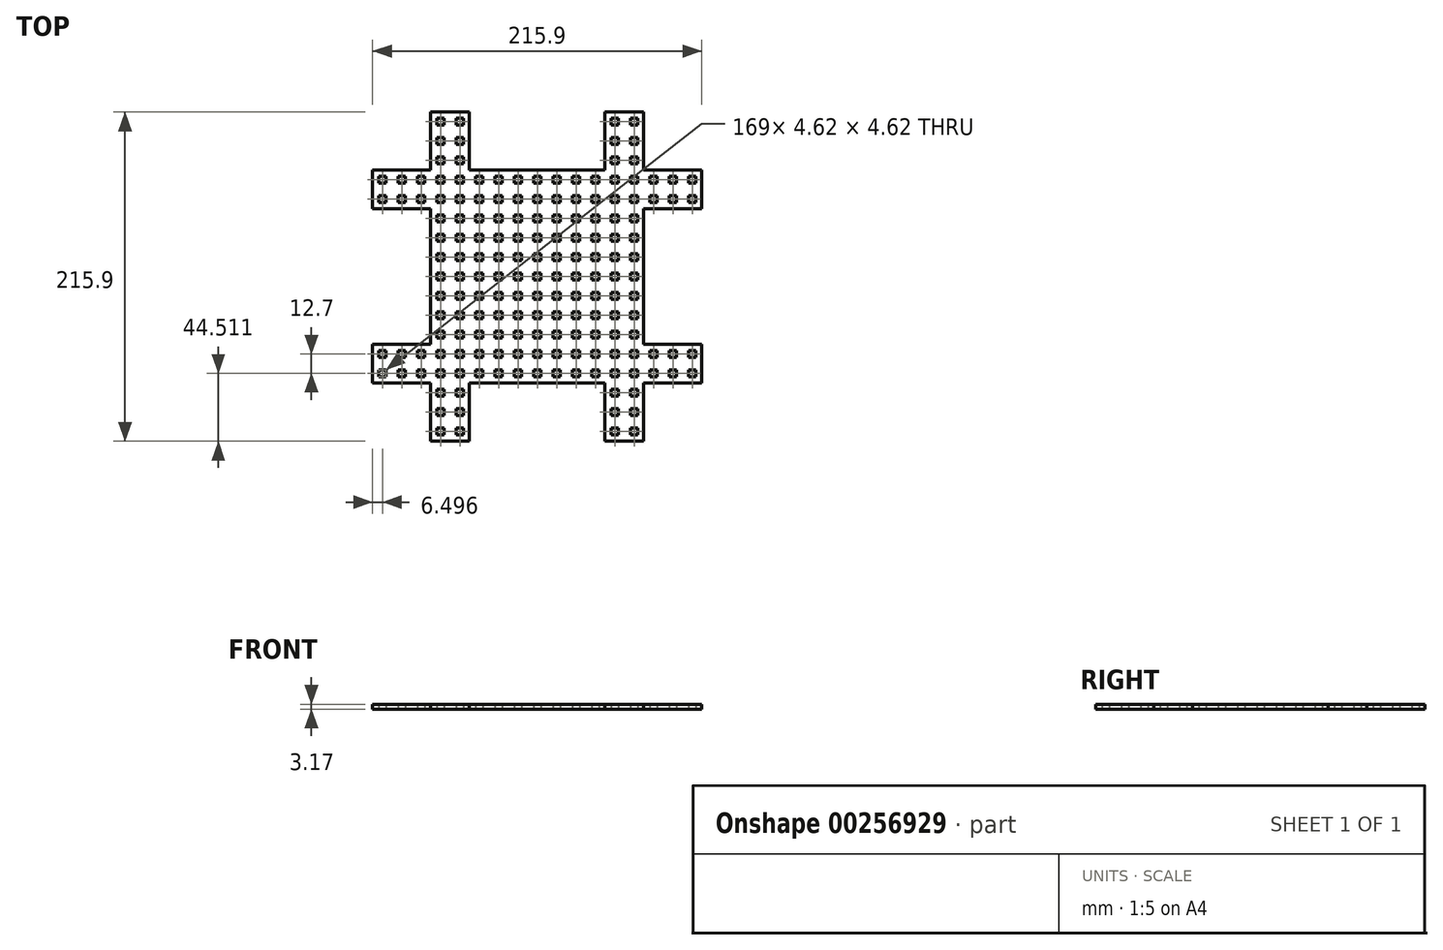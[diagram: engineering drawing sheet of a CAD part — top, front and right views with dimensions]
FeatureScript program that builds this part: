
annotation { "Feature Type Name" : "Feature", "Feature Type Description" : "" }
export const myFeature = defineFeature(function(context is Context, id is Id, definition is map)
    precondition{}
    {
        {
            var Q0;
            Q0=qCreatedBy(makeId("Top.planeOp"),FACE);
            var sketch = newSketch(context, id + "F0", { "sketchPlane" : qUnion([Q0])});
            skLineSegment(sketch, "E0.top", {"start": v(107.95, 44.45) * mm, "end": v(69.85, 44.45) * mm});
            skLineSegment(sketch, "E1.left", {"start": v(44.45, 107.95) * mm, "end": v(44.45, 69.85) * mm});
            skLineSegment(sketch, "E1.right", {"start": v(-44.45, 107.95) * mm, "end": v(-44.45, 69.85) * mm});
            skLineSegment(sketch, "E2.trimOffspring", {"start": v(-69.85, 44.45) * mm, "end": v(-107.95, 44.45) * mm});
            skLineSegment(sketch, "E3.trimOffspring", {"start": v(-69.85, -44.45) * mm, "end": v(-107.95, -44.45) * mm});
            skLineSegment(sketch, "E4.trimOffspring", {"start": v(-44.45, -69.85) * mm, "end": v(-44.45, -107.95) * mm});
            skLineSegment(sketch, "E5", {"start": v(-107.95, 44.45) * mm, "end": v(-69.85, 44.45) * mm});
            skLineSegment(sketch, "E6", {"start": v(-69.85, 69.85) * mm, "end": v(-69.85, 107.95) * mm});
            skLineSegment(sketch, "E7.bottom", {"start": v(-69.85, 107.95) * mm, "end": v(-44.45, 107.95) * mm});
            skLineSegment(sketch, "E7.top", {"start": v(-69.85, -107.95) * mm, "end": v(-44.45, -107.95) * mm});
            skLineSegment(sketch, "E7.left", {"start": v(-69.85, 107.95) * mm, "end": v(-69.85, 69.85) * mm});
            skLineSegment(sketch, "E7.right", {"start": v(69.85, 107.95) * mm, "end": v(69.85, 69.85) * mm});
            skLineSegment(sketch, "E8.bottom", {"start": v(107.95, -69.85) * mm, "end": v(69.85, -69.85) * mm});
            skLineSegment(sketch, "E8.left", {"start": v(107.95, -69.85) * mm, "end": v(107.95, -44.45) * mm});
            skLineSegment(sketch, "E9.trimOffspring", {"start": v(44.45, 107.95) * mm, "end": v(69.85, 107.95) * mm});
            skLineSegment(sketch, "E10.trimOffspring", {"start": v(44.45, 69.85) * mm, "end": v(-44.45, 69.85) * mm});
            skLineSegment(sketch, "E11.trimOffspring", {"start": v(69.85, 44.45) * mm, "end": v(69.85, -44.45) * mm});
            skLineSegment(sketch, "E12", {"start": v(69.85, 69.85) * mm, "end": v(107.95, 69.85) * mm});
            skLineSegment(sketch, "E13.trimOffspring", {"start": v(107.95, 44.45) * mm, "end": v(107.95, 69.85) * mm});
            skLineSegment(sketch, "E14.trimOffspring", {"start": v(-69.85, 69.85) * mm, "end": v(-107.95, 69.85) * mm});
            skLineSegment(sketch, "E15.trimOffspring", {"start": v(-69.85, 44.45) * mm, "end": v(-69.85, -44.45) * mm});
            skLineSegment(sketch, "E16.trimOffspring", {"start": v(-107.95, 44.45) * mm, "end": v(-107.95, 69.85) * mm});
            skLineSegment(sketch, "E17.trimOffspring", {"start": v(69.85, -69.85) * mm, "end": v(69.85, -107.95) * mm});
            skLineSegment(sketch, "E18.trimOffspring", {"start": v(44.45, -69.85) * mm, "end": v(-44.45, -69.85) * mm});
            skLineSegment(sketch, "E19", {"start": v(69.85, -44.45) * mm, "end": v(107.95, -44.45) * mm});
            skLineSegment(sketch, "E20", {"start": v(-107.95, -69.85) * mm, "end": v(-107.95, -44.45) * mm});
            skLineSegment(sketch, "E21.trimOffspring", {"start": v(-69.85, -69.85) * mm, "end": v(-69.85, -107.95) * mm});
            skLineSegment(sketch, "E22.trimOffspring", {"start": v(-69.85, -69.85) * mm, "end": v(-107.95, -69.85) * mm});
            skPoint(sketch, "E1.top.start.orphan", {"position": v(44.45, -107.95) * mm});
            skLineSegment(sketch, "E23.trimOffspring", {"start": v(44.45, -107.95) * mm, "end": v(69.85, -107.95) * mm});
            skLineSegment(sketch, "E24", {"start": v(44.45, -107.95) * mm, "end": v(44.45, -69.85) * mm});
            skLineSegment(sketch, "E25.MirrorCS", {"start": v(69.85, -69.85) * mm, "end": v(107.95, -69.85) * mm});
            skLineSegment(sketch, "E26.MirrorCS", {"start": v(107.95, -44.45) * mm, "end": v(69.85, -44.45) * mm});
            skLineSegment(sketch, "E27.MirrorCS", {"start": v(69.85, -107.95) * mm, "end": v(69.85, -69.85) * mm});
            skLineSegment(sketch, "E28.MirrorCS", {"start": v(107.95, -44.45) * mm, "end": v(107.95, -69.85) * mm});
            skLineSegment(sketch, "E29.MirrorCS", {"start": v(-44.45, -107.95) * mm, "end": v(-69.85, -107.95) * mm});
            skLineSegment(sketch, "E30.MirrorCS", {"start": v(-44.45, -107.95) * mm, "end": v(-44.45, -69.85) * mm});
            skLineSegment(sketch, "E31.MirrorCS", {"start": v(-69.85, -107.95) * mm, "end": v(-69.85, -69.85) * mm});
            skLineSegment(sketch, "E32.MirrorCS", {"start": v(-107.95, -44.45) * mm, "end": v(-69.85, -44.45) * mm});
            skLineSegment(sketch, "E33.MirrorCS", {"start": v(-107.95, -69.85) * mm, "end": v(-69.85, -69.85) * mm});
            skLineSegment(sketch, "E34.MirrorCS", {"start": v(-44.45, 107.95) * mm, "end": v(-69.85, 107.95) * mm});
            skLineSegment(sketch, "E35.MirrorCS", {"start": v(-107.95, -44.45) * mm, "end": v(-107.95, -69.85) * mm});
            skPoint(sketch, "E36", {"position": v(-101.45, -101.54) * mm});
            skLineSegment(sketch, "E37.bottom", {"start": v(-99.14, -103.85) * mm, "end": v(-103.77, -103.85) * mm});
            skLineSegment(sketch, "E37.top", {"start": v(-99.14, -99.23) * mm, "end": v(-103.77, -99.23) * mm});
            skLineSegment(sketch, "E37.left", {"start": v(-99.14, -103.85) * mm, "end": v(-99.14, -99.23) * mm});
            skLineSegment(sketch, "E37.right", {"start": v(-103.77, -103.85) * mm, "end": v(-103.77, -99.23) * mm});
            skLineSegment(sketch, "E38.0.1.0", {"start": v(-99.14, -91.15) * mm, "end": v(-103.77, -91.15) * mm});
            skLineSegment(sketch, "E38.0.1.1", {"start": v(-99.14, -91.15) * mm, "end": v(-99.14, -86.53) * mm});
            skLineSegment(sketch, "E38.0.1.2", {"start": v(-103.77, -91.15) * mm, "end": v(-103.77, -86.53) * mm});
            skLineSegment(sketch, "E38.0.1.3", {"start": v(-99.14, -86.53) * mm, "end": v(-103.77, -86.53) * mm});
            skLineSegment(sketch, "E38.0.2.0", {"start": v(-99.14, -78.45) * mm, "end": v(-103.77, -78.45) * mm});
            skLineSegment(sketch, "E38.0.2.1", {"start": v(-99.14, -78.45) * mm, "end": v(-99.14, -73.83) * mm});
            skLineSegment(sketch, "E38.0.2.2", {"start": v(-103.77, -78.45) * mm, "end": v(-103.77, -73.83) * mm});
            skLineSegment(sketch, "E38.0.2.3", {"start": v(-99.14, -73.83) * mm, "end": v(-103.77, -73.83) * mm});
            skLineSegment(sketch, "E38.0.3.0", {"start": v(-99.14, -65.75) * mm, "end": v(-103.77, -65.75) * mm});
            skLineSegment(sketch, "E38.0.3.1", {"start": v(-99.14, -65.75) * mm, "end": v(-99.14, -61.13) * mm});
            skLineSegment(sketch, "E38.0.3.2", {"start": v(-103.77, -65.75) * mm, "end": v(-103.77, -61.13) * mm});
            skLineSegment(sketch, "E38.0.3.3", {"start": v(-99.14, -61.13) * mm, "end": v(-103.77, -61.13) * mm});
            skLineSegment(sketch, "E38.0.4.0", {"start": v(-99.14, -53.05) * mm, "end": v(-103.77, -53.05) * mm});
            skLineSegment(sketch, "E38.0.4.1", {"start": v(-99.14, -53.05) * mm, "end": v(-99.14, -48.43) * mm});
            skLineSegment(sketch, "E38.0.4.2", {"start": v(-103.77, -53.05) * mm, "end": v(-103.77, -48.43) * mm});
            skLineSegment(sketch, "E38.0.4.3", {"start": v(-99.14, -48.43) * mm, "end": v(-103.77, -48.43) * mm});
            skLineSegment(sketch, "E38.0.5.0", {"start": v(-99.14, -40.35) * mm, "end": v(-103.77, -40.35) * mm});
            skLineSegment(sketch, "E38.0.5.1", {"start": v(-99.14, -40.35) * mm, "end": v(-99.14, -35.73) * mm});
            skLineSegment(sketch, "E38.0.5.2", {"start": v(-103.77, -40.35) * mm, "end": v(-103.77, -35.73) * mm});
            skLineSegment(sketch, "E38.0.5.3", {"start": v(-99.14, -35.73) * mm, "end": v(-103.77, -35.73) * mm});
            skLineSegment(sketch, "E38.0.6.0", {"start": v(-99.14, -27.65) * mm, "end": v(-103.77, -27.65) * mm});
            skLineSegment(sketch, "E38.0.6.1", {"start": v(-99.14, -27.65) * mm, "end": v(-99.14, -23.03) * mm});
            skLineSegment(sketch, "E38.0.6.2", {"start": v(-103.77, -27.65) * mm, "end": v(-103.77, -23.03) * mm});
            skLineSegment(sketch, "E38.0.6.3", {"start": v(-99.14, -23.03) * mm, "end": v(-103.77, -23.03) * mm});
            skLineSegment(sketch, "E38.0.7.0", {"start": v(-99.14, -14.95) * mm, "end": v(-103.77, -14.95) * mm});
            skLineSegment(sketch, "E38.0.7.1", {"start": v(-99.14, -14.95) * mm, "end": v(-99.14, -10.33) * mm});
            skLineSegment(sketch, "E38.0.7.2", {"start": v(-103.77, -14.95) * mm, "end": v(-103.77, -10.33) * mm});
            skLineSegment(sketch, "E38.0.7.3", {"start": v(-99.14, -10.33) * mm, "end": v(-103.77, -10.33) * mm});
            skLineSegment(sketch, "E38.0.8.0", {"start": v(-99.14, -2.25) * mm, "end": v(-103.77, -2.25) * mm});
            skLineSegment(sketch, "E38.0.8.1", {"start": v(-99.14, -2.25) * mm, "end": v(-99.14, 2.37) * mm});
            skLineSegment(sketch, "E38.0.8.2", {"start": v(-103.77, -2.25) * mm, "end": v(-103.77, 2.37) * mm});
            skLineSegment(sketch, "E38.0.8.3", {"start": v(-99.14, 2.37) * mm, "end": v(-103.77, 2.37) * mm});
            skLineSegment(sketch, "E38.0.9.0", {"start": v(-99.14, 10.45) * mm, "end": v(-103.77, 10.45) * mm});
            skLineSegment(sketch, "E38.0.9.1", {"start": v(-99.14, 10.45) * mm, "end": v(-99.14, 15.07) * mm});
            skLineSegment(sketch, "E38.0.9.2", {"start": v(-103.77, 10.45) * mm, "end": v(-103.77, 15.07) * mm});
            skLineSegment(sketch, "E38.0.9.3", {"start": v(-99.14, 15.07) * mm, "end": v(-103.77, 15.07) * mm});
            skLineSegment(sketch, "E38.0.10.0", {"start": v(-99.14, 23.15) * mm, "end": v(-103.77, 23.15) * mm});
            skLineSegment(sketch, "E38.0.10.1", {"start": v(-99.14, 23.15) * mm, "end": v(-99.14, 27.77) * mm});
            skLineSegment(sketch, "E38.0.10.2", {"start": v(-103.77, 23.15) * mm, "end": v(-103.77, 27.77) * mm});
            skLineSegment(sketch, "E38.0.10.3", {"start": v(-99.14, 27.77) * mm, "end": v(-103.77, 27.77) * mm});
            skLineSegment(sketch, "E38.0.11.0", {"start": v(-99.14, 35.85) * mm, "end": v(-103.77, 35.85) * mm});
            skLineSegment(sketch, "E38.0.11.1", {"start": v(-99.14, 35.85) * mm, "end": v(-99.14, 40.47) * mm});
            skLineSegment(sketch, "E38.0.11.2", {"start": v(-103.77, 35.85) * mm, "end": v(-103.77, 40.47) * mm});
            skLineSegment(sketch, "E38.0.11.3", {"start": v(-99.14, 40.47) * mm, "end": v(-103.77, 40.47) * mm});
            skLineSegment(sketch, "E38.0.12.0", {"start": v(-99.14, 48.55) * mm, "end": v(-103.77, 48.55) * mm});
            skLineSegment(sketch, "E38.0.12.1", {"start": v(-99.14, 48.55) * mm, "end": v(-99.14, 53.17) * mm});
            skLineSegment(sketch, "E38.0.12.2", {"start": v(-103.77, 48.55) * mm, "end": v(-103.77, 53.17) * mm});
            skLineSegment(sketch, "E38.0.12.3", {"start": v(-99.14, 53.17) * mm, "end": v(-103.77, 53.17) * mm});
            skLineSegment(sketch, "E38.0.13.0", {"start": v(-99.14, 61.25) * mm, "end": v(-103.77, 61.25) * mm});
            skLineSegment(sketch, "E38.0.13.1", {"start": v(-99.14, 61.25) * mm, "end": v(-99.14, 65.87) * mm});
            skLineSegment(sketch, "E38.0.13.2", {"start": v(-103.77, 61.25) * mm, "end": v(-103.77, 65.87) * mm});
            skLineSegment(sketch, "E38.0.13.3", {"start": v(-99.14, 65.87) * mm, "end": v(-103.77, 65.87) * mm});
            skLineSegment(sketch, "E38.0.14.0", {"start": v(-99.14, 73.95) * mm, "end": v(-103.77, 73.95) * mm});
            skLineSegment(sketch, "E38.0.14.1", {"start": v(-99.14, 73.95) * mm, "end": v(-99.14, 78.57) * mm});
            skLineSegment(sketch, "E38.0.14.2", {"start": v(-103.77, 73.95) * mm, "end": v(-103.77, 78.57) * mm});
            skLineSegment(sketch, "E38.0.14.3", {"start": v(-99.14, 78.57) * mm, "end": v(-103.77, 78.57) * mm});
            skLineSegment(sketch, "E38.0.15.0", {"start": v(-99.14, 86.65) * mm, "end": v(-103.77, 86.65) * mm});
            skLineSegment(sketch, "E38.0.15.1", {"start": v(-99.14, 86.65) * mm, "end": v(-99.14, 91.27) * mm});
            skLineSegment(sketch, "E38.0.15.2", {"start": v(-103.77, 86.65) * mm, "end": v(-103.77, 91.27) * mm});
            skLineSegment(sketch, "E38.0.15.3", {"start": v(-99.14, 91.27) * mm, "end": v(-103.77, 91.27) * mm});
            skLineSegment(sketch, "E38.0.16.0", {"start": v(-99.14, 99.35) * mm, "end": v(-103.77, 99.35) * mm});
            skLineSegment(sketch, "E38.0.16.1", {"start": v(-99.14, 99.35) * mm, "end": v(-99.14, 103.97) * mm});
            skLineSegment(sketch, "E38.0.16.2", {"start": v(-103.77, 99.35) * mm, "end": v(-103.77, 103.97) * mm});
            skLineSegment(sketch, "E38.0.16.3", {"start": v(-99.14, 103.97) * mm, "end": v(-103.77, 103.97) * mm});
            skLineSegment(sketch, "E38.1.0.0", {"start": v(-86.44, -103.85) * mm, "end": v(-91.07, -103.85) * mm});
            skLineSegment(sketch, "E38.1.0.1", {"start": v(-86.44, -103.85) * mm, "end": v(-86.44, -99.23) * mm});
            skLineSegment(sketch, "E38.1.0.2", {"start": v(-91.07, -103.85) * mm, "end": v(-91.07, -99.23) * mm});
            skLineSegment(sketch, "E38.1.0.3", {"start": v(-86.44, -99.23) * mm, "end": v(-91.07, -99.23) * mm});
            skLineSegment(sketch, "E38.1.1.0", {"start": v(-86.44, -91.15) * mm, "end": v(-91.07, -91.15) * mm});
            skLineSegment(sketch, "E38.1.1.1", {"start": v(-86.44, -91.15) * mm, "end": v(-86.44, -86.53) * mm});
            skLineSegment(sketch, "E38.1.1.2", {"start": v(-91.07, -91.15) * mm, "end": v(-91.07, -86.53) * mm});
            skLineSegment(sketch, "E38.1.1.3", {"start": v(-86.44, -86.53) * mm, "end": v(-91.07, -86.53) * mm});
            skLineSegment(sketch, "E38.1.2.0", {"start": v(-86.44, -78.45) * mm, "end": v(-91.07, -78.45) * mm});
            skLineSegment(sketch, "E38.1.2.1", {"start": v(-86.44, -78.45) * mm, "end": v(-86.44, -73.83) * mm});
            skLineSegment(sketch, "E38.1.2.2", {"start": v(-91.07, -78.45) * mm, "end": v(-91.07, -73.83) * mm});
            skLineSegment(sketch, "E38.1.2.3", {"start": v(-86.44, -73.83) * mm, "end": v(-91.07, -73.83) * mm});
            skLineSegment(sketch, "E38.1.3.0", {"start": v(-86.44, -65.75) * mm, "end": v(-91.07, -65.75) * mm});
            skLineSegment(sketch, "E38.1.3.1", {"start": v(-86.44, -65.75) * mm, "end": v(-86.44, -61.13) * mm});
            skLineSegment(sketch, "E38.1.3.2", {"start": v(-91.07, -65.75) * mm, "end": v(-91.07, -61.13) * mm});
            skLineSegment(sketch, "E38.1.3.3", {"start": v(-86.44, -61.13) * mm, "end": v(-91.07, -61.13) * mm});
            skLineSegment(sketch, "E38.1.4.0", {"start": v(-86.44, -53.05) * mm, "end": v(-91.07, -53.05) * mm});
            skLineSegment(sketch, "E38.1.4.1", {"start": v(-86.44, -53.05) * mm, "end": v(-86.44, -48.43) * mm});
            skLineSegment(sketch, "E38.1.4.2", {"start": v(-91.07, -53.05) * mm, "end": v(-91.07, -48.43) * mm});
            skLineSegment(sketch, "E38.1.4.3", {"start": v(-86.44, -48.43) * mm, "end": v(-91.07, -48.43) * mm});
            skLineSegment(sketch, "E38.1.5.0", {"start": v(-86.44, -40.35) * mm, "end": v(-91.07, -40.35) * mm});
            skLineSegment(sketch, "E38.1.5.1", {"start": v(-86.44, -40.35) * mm, "end": v(-86.44, -35.73) * mm});
            skLineSegment(sketch, "E38.1.5.2", {"start": v(-91.07, -40.35) * mm, "end": v(-91.07, -35.73) * mm});
            skLineSegment(sketch, "E38.1.5.3", {"start": v(-86.44, -35.73) * mm, "end": v(-91.07, -35.73) * mm});
            skLineSegment(sketch, "E38.1.6.0", {"start": v(-86.44, -27.65) * mm, "end": v(-91.07, -27.65) * mm});
            skLineSegment(sketch, "E38.1.6.1", {"start": v(-86.44, -27.65) * mm, "end": v(-86.44, -23.03) * mm});
            skLineSegment(sketch, "E38.1.6.2", {"start": v(-91.07, -27.65) * mm, "end": v(-91.07, -23.03) * mm});
            skLineSegment(sketch, "E38.1.6.3", {"start": v(-86.44, -23.03) * mm, "end": v(-91.07, -23.03) * mm});
            skLineSegment(sketch, "E38.1.7.0", {"start": v(-86.44, -14.95) * mm, "end": v(-91.07, -14.95) * mm});
            skLineSegment(sketch, "E38.1.7.1", {"start": v(-86.44, -14.95) * mm, "end": v(-86.44, -10.33) * mm});
            skLineSegment(sketch, "E38.1.7.2", {"start": v(-91.07, -14.95) * mm, "end": v(-91.07, -10.33) * mm});
            skLineSegment(sketch, "E38.1.7.3", {"start": v(-86.44, -10.33) * mm, "end": v(-91.07, -10.33) * mm});
            skLineSegment(sketch, "E38.1.8.0", {"start": v(-86.44, -2.25) * mm, "end": v(-91.07, -2.25) * mm});
            skLineSegment(sketch, "E38.1.8.1", {"start": v(-86.44, -2.25) * mm, "end": v(-86.44, 2.37) * mm});
            skLineSegment(sketch, "E38.1.8.2", {"start": v(-91.07, -2.25) * mm, "end": v(-91.07, 2.37) * mm});
            skLineSegment(sketch, "E38.1.8.3", {"start": v(-86.44, 2.37) * mm, "end": v(-91.07, 2.37) * mm});
            skLineSegment(sketch, "E38.1.9.0", {"start": v(-86.44, 10.45) * mm, "end": v(-91.07, 10.45) * mm});
            skLineSegment(sketch, "E38.1.9.1", {"start": v(-86.44, 10.45) * mm, "end": v(-86.44, 15.07) * mm});
            skLineSegment(sketch, "E38.1.9.2", {"start": v(-91.07, 10.45) * mm, "end": v(-91.07, 15.07) * mm});
            skLineSegment(sketch, "E38.1.9.3", {"start": v(-86.44, 15.07) * mm, "end": v(-91.07, 15.07) * mm});
            skLineSegment(sketch, "E38.1.10.0", {"start": v(-86.44, 23.15) * mm, "end": v(-91.07, 23.15) * mm});
            skLineSegment(sketch, "E38.1.10.1", {"start": v(-86.44, 23.15) * mm, "end": v(-86.44, 27.77) * mm});
            skLineSegment(sketch, "E38.1.10.2", {"start": v(-91.07, 23.15) * mm, "end": v(-91.07, 27.77) * mm});
            skLineSegment(sketch, "E38.1.10.3", {"start": v(-86.44, 27.77) * mm, "end": v(-91.07, 27.77) * mm});
            skLineSegment(sketch, "E38.1.11.0", {"start": v(-86.44, 35.85) * mm, "end": v(-91.07, 35.85) * mm});
            skLineSegment(sketch, "E38.1.11.1", {"start": v(-86.44, 35.85) * mm, "end": v(-86.44, 40.47) * mm});
            skLineSegment(sketch, "E38.1.11.2", {"start": v(-91.07, 35.85) * mm, "end": v(-91.07, 40.47) * mm});
            skLineSegment(sketch, "E38.1.11.3", {"start": v(-86.44, 40.47) * mm, "end": v(-91.07, 40.47) * mm});
            skLineSegment(sketch, "E38.1.12.0", {"start": v(-86.44, 48.55) * mm, "end": v(-91.07, 48.55) * mm});
            skLineSegment(sketch, "E38.1.12.1", {"start": v(-86.44, 48.55) * mm, "end": v(-86.44, 53.17) * mm});
            skLineSegment(sketch, "E38.1.12.2", {"start": v(-91.07, 48.55) * mm, "end": v(-91.07, 53.17) * mm});
            skLineSegment(sketch, "E38.1.12.3", {"start": v(-86.44, 53.17) * mm, "end": v(-91.07, 53.17) * mm});
            skLineSegment(sketch, "E38.1.13.0", {"start": v(-86.44, 61.25) * mm, "end": v(-91.07, 61.25) * mm});
            skLineSegment(sketch, "E38.1.13.1", {"start": v(-86.44, 61.25) * mm, "end": v(-86.44, 65.87) * mm});
            skLineSegment(sketch, "E38.1.13.2", {"start": v(-91.07, 61.25) * mm, "end": v(-91.07, 65.87) * mm});
            skLineSegment(sketch, "E38.1.13.3", {"start": v(-86.44, 65.87) * mm, "end": v(-91.07, 65.87) * mm});
            skLineSegment(sketch, "E38.1.14.0", {"start": v(-86.44, 73.95) * mm, "end": v(-91.07, 73.95) * mm});
            skLineSegment(sketch, "E38.1.14.1", {"start": v(-86.44, 73.95) * mm, "end": v(-86.44, 78.57) * mm});
            skLineSegment(sketch, "E38.1.14.2", {"start": v(-91.07, 73.95) * mm, "end": v(-91.07, 78.57) * mm});
            skLineSegment(sketch, "E38.1.14.3", {"start": v(-86.44, 78.57) * mm, "end": v(-91.07, 78.57) * mm});
            skLineSegment(sketch, "E38.1.15.0", {"start": v(-86.44, 86.65) * mm, "end": v(-91.07, 86.65) * mm});
            skLineSegment(sketch, "E38.1.15.1", {"start": v(-86.44, 86.65) * mm, "end": v(-86.44, 91.27) * mm});
            skLineSegment(sketch, "E38.1.15.2", {"start": v(-91.07, 86.65) * mm, "end": v(-91.07, 91.27) * mm});
            skLineSegment(sketch, "E38.1.15.3", {"start": v(-86.44, 91.27) * mm, "end": v(-91.07, 91.27) * mm});
            skLineSegment(sketch, "E38.1.16.0", {"start": v(-86.44, 99.35) * mm, "end": v(-91.07, 99.35) * mm});
            skLineSegment(sketch, "E38.1.16.1", {"start": v(-86.44, 99.35) * mm, "end": v(-86.44, 103.97) * mm});
            skLineSegment(sketch, "E38.1.16.2", {"start": v(-91.07, 99.35) * mm, "end": v(-91.07, 103.97) * mm});
            skLineSegment(sketch, "E38.1.16.3", {"start": v(-86.44, 103.97) * mm, "end": v(-91.07, 103.97) * mm});
            skLineSegment(sketch, "E38.2.0.0", {"start": v(-73.74, -103.85) * mm, "end": v(-78.37, -103.85) * mm});
            skLineSegment(sketch, "E38.2.0.1", {"start": v(-73.74, -103.85) * mm, "end": v(-73.74, -99.23) * mm});
            skLineSegment(sketch, "E38.2.0.2", {"start": v(-78.37, -103.85) * mm, "end": v(-78.37, -99.23) * mm});
            skLineSegment(sketch, "E38.2.0.3", {"start": v(-73.74, -99.23) * mm, "end": v(-78.37, -99.23) * mm});
            skLineSegment(sketch, "E38.2.1.0", {"start": v(-73.74, -91.15) * mm, "end": v(-78.37, -91.15) * mm});
            skLineSegment(sketch, "E38.2.1.1", {"start": v(-73.74, -91.15) * mm, "end": v(-73.74, -86.53) * mm});
            skLineSegment(sketch, "E38.2.1.2", {"start": v(-78.37, -91.15) * mm, "end": v(-78.37, -86.53) * mm});
            skLineSegment(sketch, "E38.2.1.3", {"start": v(-73.74, -86.53) * mm, "end": v(-78.37, -86.53) * mm});
            skLineSegment(sketch, "E38.2.2.0", {"start": v(-73.74, -78.45) * mm, "end": v(-78.37, -78.45) * mm});
            skLineSegment(sketch, "E38.2.2.1", {"start": v(-73.74, -78.45) * mm, "end": v(-73.74, -73.83) * mm});
            skLineSegment(sketch, "E38.2.2.2", {"start": v(-78.37, -78.45) * mm, "end": v(-78.37, -73.83) * mm});
            skLineSegment(sketch, "E38.2.2.3", {"start": v(-73.74, -73.83) * mm, "end": v(-78.37, -73.83) * mm});
            skLineSegment(sketch, "E38.2.3.0", {"start": v(-73.74, -65.75) * mm, "end": v(-78.37, -65.75) * mm});
            skLineSegment(sketch, "E38.2.3.1", {"start": v(-73.74, -65.75) * mm, "end": v(-73.74, -61.13) * mm});
            skLineSegment(sketch, "E38.2.3.2", {"start": v(-78.37, -65.75) * mm, "end": v(-78.37, -61.13) * mm});
            skLineSegment(sketch, "E38.2.3.3", {"start": v(-73.74, -61.13) * mm, "end": v(-78.37, -61.13) * mm});
            skLineSegment(sketch, "E38.2.4.0", {"start": v(-73.74, -53.05) * mm, "end": v(-78.37, -53.05) * mm});
            skLineSegment(sketch, "E38.2.4.1", {"start": v(-73.74, -53.05) * mm, "end": v(-73.74, -48.43) * mm});
            skLineSegment(sketch, "E38.2.4.2", {"start": v(-78.37, -53.05) * mm, "end": v(-78.37, -48.43) * mm});
            skLineSegment(sketch, "E38.2.4.3", {"start": v(-73.74, -48.43) * mm, "end": v(-78.37, -48.43) * mm});
            skLineSegment(sketch, "E38.2.5.0", {"start": v(-73.74, -40.35) * mm, "end": v(-78.37, -40.35) * mm});
            skLineSegment(sketch, "E38.2.5.1", {"start": v(-73.74, -40.35) * mm, "end": v(-73.74, -35.73) * mm});
            skLineSegment(sketch, "E38.2.5.2", {"start": v(-78.37, -40.35) * mm, "end": v(-78.37, -35.73) * mm});
            skLineSegment(sketch, "E38.2.5.3", {"start": v(-73.74, -35.73) * mm, "end": v(-78.37, -35.73) * mm});
            skLineSegment(sketch, "E38.2.6.0", {"start": v(-73.74, -27.65) * mm, "end": v(-78.37, -27.65) * mm});
            skLineSegment(sketch, "E38.2.6.1", {"start": v(-73.74, -27.65) * mm, "end": v(-73.74, -23.03) * mm});
            skLineSegment(sketch, "E38.2.6.2", {"start": v(-78.37, -27.65) * mm, "end": v(-78.37, -23.03) * mm});
            skLineSegment(sketch, "E38.2.6.3", {"start": v(-73.74, -23.03) * mm, "end": v(-78.37, -23.03) * mm});
            skLineSegment(sketch, "E38.2.7.0", {"start": v(-73.74, -14.95) * mm, "end": v(-78.37, -14.95) * mm});
            skLineSegment(sketch, "E38.2.7.1", {"start": v(-73.74, -14.95) * mm, "end": v(-73.74, -10.33) * mm});
            skLineSegment(sketch, "E38.2.7.2", {"start": v(-78.37, -14.95) * mm, "end": v(-78.37, -10.33) * mm});
            skLineSegment(sketch, "E38.2.7.3", {"start": v(-73.74, -10.33) * mm, "end": v(-78.37, -10.33) * mm});
            skLineSegment(sketch, "E38.2.8.0", {"start": v(-73.74, -2.25) * mm, "end": v(-78.37, -2.25) * mm});
            skLineSegment(sketch, "E38.2.8.1", {"start": v(-73.74, -2.25) * mm, "end": v(-73.74, 2.37) * mm});
            skLineSegment(sketch, "E38.2.8.2", {"start": v(-78.37, -2.25) * mm, "end": v(-78.37, 2.37) * mm});
            skLineSegment(sketch, "E38.2.8.3", {"start": v(-73.74, 2.37) * mm, "end": v(-78.37, 2.37) * mm});
            skLineSegment(sketch, "E38.2.9.0", {"start": v(-73.74, 10.45) * mm, "end": v(-78.37, 10.45) * mm});
            skLineSegment(sketch, "E38.2.9.1", {"start": v(-73.74, 10.45) * mm, "end": v(-73.74, 15.07) * mm});
            skLineSegment(sketch, "E38.2.9.2", {"start": v(-78.37, 10.45) * mm, "end": v(-78.37, 15.07) * mm});
            skLineSegment(sketch, "E38.2.9.3", {"start": v(-73.74, 15.07) * mm, "end": v(-78.37, 15.07) * mm});
            skLineSegment(sketch, "E38.2.10.0", {"start": v(-73.74, 23.15) * mm, "end": v(-78.37, 23.15) * mm});
            skLineSegment(sketch, "E38.2.10.1", {"start": v(-73.74, 23.15) * mm, "end": v(-73.74, 27.77) * mm});
            skLineSegment(sketch, "E38.2.10.2", {"start": v(-78.37, 23.15) * mm, "end": v(-78.37, 27.77) * mm});
            skLineSegment(sketch, "E38.2.10.3", {"start": v(-73.74, 27.77) * mm, "end": v(-78.37, 27.77) * mm});
            skLineSegment(sketch, "E38.2.11.0", {"start": v(-73.74, 35.85) * mm, "end": v(-78.37, 35.85) * mm});
            skLineSegment(sketch, "E38.2.11.1", {"start": v(-73.74, 35.85) * mm, "end": v(-73.74, 40.47) * mm});
            skLineSegment(sketch, "E38.2.11.2", {"start": v(-78.37, 35.85) * mm, "end": v(-78.37, 40.47) * mm});
            skLineSegment(sketch, "E38.2.11.3", {"start": v(-73.74, 40.47) * mm, "end": v(-78.37, 40.47) * mm});
            skLineSegment(sketch, "E38.2.12.0", {"start": v(-73.74, 48.55) * mm, "end": v(-78.37, 48.55) * mm});
            skLineSegment(sketch, "E38.2.12.1", {"start": v(-73.74, 48.55) * mm, "end": v(-73.74, 53.17) * mm});
            skLineSegment(sketch, "E38.2.12.2", {"start": v(-78.37, 48.55) * mm, "end": v(-78.37, 53.17) * mm});
            skLineSegment(sketch, "E38.2.12.3", {"start": v(-73.74, 53.17) * mm, "end": v(-78.37, 53.17) * mm});
            skLineSegment(sketch, "E38.2.13.0", {"start": v(-73.74, 61.25) * mm, "end": v(-78.37, 61.25) * mm});
            skLineSegment(sketch, "E38.2.13.1", {"start": v(-73.74, 61.25) * mm, "end": v(-73.74, 65.87) * mm});
            skLineSegment(sketch, "E38.2.13.2", {"start": v(-78.37, 61.25) * mm, "end": v(-78.37, 65.87) * mm});
            skLineSegment(sketch, "E38.2.13.3", {"start": v(-73.74, 65.87) * mm, "end": v(-78.37, 65.87) * mm});
            skLineSegment(sketch, "E38.2.14.0", {"start": v(-73.74, 73.95) * mm, "end": v(-78.37, 73.95) * mm});
            skLineSegment(sketch, "E38.2.14.1", {"start": v(-73.74, 73.95) * mm, "end": v(-73.74, 78.57) * mm});
            skLineSegment(sketch, "E38.2.14.2", {"start": v(-78.37, 73.95) * mm, "end": v(-78.37, 78.57) * mm});
            skLineSegment(sketch, "E38.2.14.3", {"start": v(-73.74, 78.57) * mm, "end": v(-78.37, 78.57) * mm});
            skLineSegment(sketch, "E38.2.15.0", {"start": v(-73.74, 86.65) * mm, "end": v(-78.37, 86.65) * mm});
            skLineSegment(sketch, "E38.2.15.1", {"start": v(-73.74, 86.65) * mm, "end": v(-73.74, 91.27) * mm});
            skLineSegment(sketch, "E38.2.15.2", {"start": v(-78.37, 86.65) * mm, "end": v(-78.37, 91.27) * mm});
            skLineSegment(sketch, "E38.2.15.3", {"start": v(-73.74, 91.27) * mm, "end": v(-78.37, 91.27) * mm});
            skLineSegment(sketch, "E38.2.16.0", {"start": v(-73.74, 99.35) * mm, "end": v(-78.37, 99.35) * mm});
            skLineSegment(sketch, "E38.2.16.1", {"start": v(-73.74, 99.35) * mm, "end": v(-73.74, 103.97) * mm});
            skLineSegment(sketch, "E38.2.16.2", {"start": v(-78.37, 99.35) * mm, "end": v(-78.37, 103.97) * mm});
            skLineSegment(sketch, "E38.2.16.3", {"start": v(-73.74, 103.97) * mm, "end": v(-78.37, 103.97) * mm});
            skLineSegment(sketch, "E38.3.0.0", {"start": v(-61.04, -103.85) * mm, "end": v(-65.67, -103.85) * mm});
            skLineSegment(sketch, "E38.3.0.1", {"start": v(-61.04, -103.85) * mm, "end": v(-61.04, -99.23) * mm});
            skLineSegment(sketch, "E38.3.0.2", {"start": v(-65.67, -103.85) * mm, "end": v(-65.67, -99.23) * mm});
            skLineSegment(sketch, "E38.3.0.3", {"start": v(-61.04, -99.23) * mm, "end": v(-65.67, -99.23) * mm});
            skLineSegment(sketch, "E38.3.1.0", {"start": v(-61.04, -91.15) * mm, "end": v(-65.67, -91.15) * mm});
            skLineSegment(sketch, "E38.3.1.1", {"start": v(-61.04, -91.15) * mm, "end": v(-61.04, -86.53) * mm});
            skLineSegment(sketch, "E38.3.1.2", {"start": v(-65.67, -91.15) * mm, "end": v(-65.67, -86.53) * mm});
            skLineSegment(sketch, "E38.3.1.3", {"start": v(-61.04, -86.53) * mm, "end": v(-65.67, -86.53) * mm});
            skLineSegment(sketch, "E38.3.2.0", {"start": v(-61.04, -78.45) * mm, "end": v(-65.67, -78.45) * mm});
            skLineSegment(sketch, "E38.3.2.1", {"start": v(-61.04, -78.45) * mm, "end": v(-61.04, -73.83) * mm});
            skLineSegment(sketch, "E38.3.2.2", {"start": v(-65.67, -78.45) * mm, "end": v(-65.67, -73.83) * mm});
            skLineSegment(sketch, "E38.3.2.3", {"start": v(-61.04, -73.83) * mm, "end": v(-65.67, -73.83) * mm});
            skLineSegment(sketch, "E38.3.3.0", {"start": v(-61.04, -65.75) * mm, "end": v(-65.67, -65.75) * mm});
            skLineSegment(sketch, "E38.3.3.1", {"start": v(-61.04, -65.75) * mm, "end": v(-61.04, -61.13) * mm});
            skLineSegment(sketch, "E38.3.3.2", {"start": v(-65.67, -65.75) * mm, "end": v(-65.67, -61.13) * mm});
            skLineSegment(sketch, "E38.3.3.3", {"start": v(-61.04, -61.13) * mm, "end": v(-65.67, -61.13) * mm});
            skLineSegment(sketch, "E38.3.4.0", {"start": v(-61.04, -53.05) * mm, "end": v(-65.67, -53.05) * mm});
            skLineSegment(sketch, "E38.3.4.1", {"start": v(-61.04, -53.05) * mm, "end": v(-61.04, -48.43) * mm});
            skLineSegment(sketch, "E38.3.4.2", {"start": v(-65.67, -53.05) * mm, "end": v(-65.67, -48.43) * mm});
            skLineSegment(sketch, "E38.3.4.3", {"start": v(-61.04, -48.43) * mm, "end": v(-65.67, -48.43) * mm});
            skLineSegment(sketch, "E38.3.5.0", {"start": v(-61.04, -40.35) * mm, "end": v(-65.67, -40.35) * mm});
            skLineSegment(sketch, "E38.3.5.1", {"start": v(-61.04, -40.35) * mm, "end": v(-61.04, -35.73) * mm});
            skLineSegment(sketch, "E38.3.5.2", {"start": v(-65.67, -40.35) * mm, "end": v(-65.67, -35.73) * mm});
            skLineSegment(sketch, "E38.3.5.3", {"start": v(-61.04, -35.73) * mm, "end": v(-65.67, -35.73) * mm});
            skLineSegment(sketch, "E38.3.6.0", {"start": v(-61.04, -27.65) * mm, "end": v(-65.67, -27.65) * mm});
            skLineSegment(sketch, "E38.3.6.1", {"start": v(-61.04, -27.65) * mm, "end": v(-61.04, -23.03) * mm});
            skLineSegment(sketch, "E38.3.6.2", {"start": v(-65.67, -27.65) * mm, "end": v(-65.67, -23.03) * mm});
            skLineSegment(sketch, "E38.3.6.3", {"start": v(-61.04, -23.03) * mm, "end": v(-65.67, -23.03) * mm});
            skLineSegment(sketch, "E38.3.7.0", {"start": v(-61.04, -14.95) * mm, "end": v(-65.67, -14.95) * mm});
            skLineSegment(sketch, "E38.3.7.1", {"start": v(-61.04, -14.95) * mm, "end": v(-61.04, -10.33) * mm});
            skLineSegment(sketch, "E38.3.7.2", {"start": v(-65.67, -14.95) * mm, "end": v(-65.67, -10.33) * mm});
            skLineSegment(sketch, "E38.3.7.3", {"start": v(-61.04, -10.33) * mm, "end": v(-65.67, -10.33) * mm});
            skLineSegment(sketch, "E38.3.8.0", {"start": v(-61.04, -2.25) * mm, "end": v(-65.67, -2.25) * mm});
            skLineSegment(sketch, "E38.3.8.1", {"start": v(-61.04, -2.25) * mm, "end": v(-61.04, 2.37) * mm});
            skLineSegment(sketch, "E38.3.8.2", {"start": v(-65.67, -2.25) * mm, "end": v(-65.67, 2.37) * mm});
            skLineSegment(sketch, "E38.3.8.3", {"start": v(-61.04, 2.37) * mm, "end": v(-65.67, 2.37) * mm});
            skLineSegment(sketch, "E38.3.9.0", {"start": v(-61.04, 10.45) * mm, "end": v(-65.67, 10.45) * mm});
            skLineSegment(sketch, "E38.3.9.1", {"start": v(-61.04, 10.45) * mm, "end": v(-61.04, 15.07) * mm});
            skLineSegment(sketch, "E38.3.9.2", {"start": v(-65.67, 10.45) * mm, "end": v(-65.67, 15.07) * mm});
            skLineSegment(sketch, "E38.3.9.3", {"start": v(-61.04, 15.07) * mm, "end": v(-65.67, 15.07) * mm});
            skLineSegment(sketch, "E38.3.10.0", {"start": v(-61.04, 23.15) * mm, "end": v(-65.67, 23.15) * mm});
            skLineSegment(sketch, "E38.3.10.1", {"start": v(-61.04, 23.15) * mm, "end": v(-61.04, 27.77) * mm});
            skLineSegment(sketch, "E38.3.10.2", {"start": v(-65.67, 23.15) * mm, "end": v(-65.67, 27.77) * mm});
            skLineSegment(sketch, "E38.3.10.3", {"start": v(-61.04, 27.77) * mm, "end": v(-65.67, 27.77) * mm});
            skLineSegment(sketch, "E38.3.11.0", {"start": v(-61.04, 35.85) * mm, "end": v(-65.67, 35.85) * mm});
            skLineSegment(sketch, "E38.3.11.1", {"start": v(-61.04, 35.85) * mm, "end": v(-61.04, 40.47) * mm});
            skLineSegment(sketch, "E38.3.11.2", {"start": v(-65.67, 35.85) * mm, "end": v(-65.67, 40.47) * mm});
            skLineSegment(sketch, "E38.3.11.3", {"start": v(-61.04, 40.47) * mm, "end": v(-65.67, 40.47) * mm});
            skLineSegment(sketch, "E38.3.12.0", {"start": v(-61.04, 48.55) * mm, "end": v(-65.67, 48.55) * mm});
            skLineSegment(sketch, "E38.3.12.1", {"start": v(-61.04, 48.55) * mm, "end": v(-61.04, 53.17) * mm});
            skLineSegment(sketch, "E38.3.12.2", {"start": v(-65.67, 48.55) * mm, "end": v(-65.67, 53.17) * mm});
            skLineSegment(sketch, "E38.3.12.3", {"start": v(-61.04, 53.17) * mm, "end": v(-65.67, 53.17) * mm});
            skLineSegment(sketch, "E38.3.13.0", {"start": v(-61.04, 61.25) * mm, "end": v(-65.67, 61.25) * mm});
            skLineSegment(sketch, "E38.3.13.1", {"start": v(-61.04, 61.25) * mm, "end": v(-61.04, 65.87) * mm});
            skLineSegment(sketch, "E38.3.13.2", {"start": v(-65.67, 61.25) * mm, "end": v(-65.67, 65.87) * mm});
            skLineSegment(sketch, "E38.3.13.3", {"start": v(-61.04, 65.87) * mm, "end": v(-65.67, 65.87) * mm});
            skLineSegment(sketch, "E38.3.14.0", {"start": v(-61.04, 73.95) * mm, "end": v(-65.67, 73.95) * mm});
            skLineSegment(sketch, "E38.3.14.1", {"start": v(-61.04, 73.95) * mm, "end": v(-61.04, 78.57) * mm});
            skLineSegment(sketch, "E38.3.14.2", {"start": v(-65.67, 73.95) * mm, "end": v(-65.67, 78.57) * mm});
            skLineSegment(sketch, "E38.3.14.3", {"start": v(-61.04, 78.57) * mm, "end": v(-65.67, 78.57) * mm});
            skLineSegment(sketch, "E38.3.15.0", {"start": v(-61.04, 86.65) * mm, "end": v(-65.67, 86.65) * mm});
            skLineSegment(sketch, "E38.3.15.1", {"start": v(-61.04, 86.65) * mm, "end": v(-61.04, 91.27) * mm});
            skLineSegment(sketch, "E38.3.15.2", {"start": v(-65.67, 86.65) * mm, "end": v(-65.67, 91.27) * mm});
            skLineSegment(sketch, "E38.3.15.3", {"start": v(-61.04, 91.27) * mm, "end": v(-65.67, 91.27) * mm});
            skLineSegment(sketch, "E38.3.16.0", {"start": v(-61.04, 99.35) * mm, "end": v(-65.67, 99.35) * mm});
            skLineSegment(sketch, "E38.3.16.1", {"start": v(-61.04, 99.35) * mm, "end": v(-61.04, 103.97) * mm});
            skLineSegment(sketch, "E38.3.16.2", {"start": v(-65.67, 99.35) * mm, "end": v(-65.67, 103.97) * mm});
            skLineSegment(sketch, "E38.3.16.3", {"start": v(-61.04, 103.97) * mm, "end": v(-65.67, 103.97) * mm});
            skLineSegment(sketch, "E38.4.0.0", {"start": v(-48.34, -103.85) * mm, "end": v(-52.97, -103.85) * mm});
            skLineSegment(sketch, "E38.4.0.1", {"start": v(-48.34, -103.85) * mm, "end": v(-48.34, -99.23) * mm});
            skLineSegment(sketch, "E38.4.0.2", {"start": v(-52.97, -103.85) * mm, "end": v(-52.97, -99.23) * mm});
            skLineSegment(sketch, "E38.4.0.3", {"start": v(-48.34, -99.23) * mm, "end": v(-52.97, -99.23) * mm});
            skLineSegment(sketch, "E38.4.1.0", {"start": v(-48.34, -91.15) * mm, "end": v(-52.97, -91.15) * mm});
            skLineSegment(sketch, "E38.4.1.1", {"start": v(-48.34, -91.15) * mm, "end": v(-48.34, -86.53) * mm});
            skLineSegment(sketch, "E38.4.1.2", {"start": v(-52.97, -91.15) * mm, "end": v(-52.97, -86.53) * mm});
            skLineSegment(sketch, "E38.4.1.3", {"start": v(-48.34, -86.53) * mm, "end": v(-52.97, -86.53) * mm});
            skLineSegment(sketch, "E38.4.2.0", {"start": v(-48.34, -78.45) * mm, "end": v(-52.97, -78.45) * mm});
            skLineSegment(sketch, "E38.4.2.1", {"start": v(-48.34, -78.45) * mm, "end": v(-48.34, -73.83) * mm});
            skLineSegment(sketch, "E38.4.2.2", {"start": v(-52.97, -78.45) * mm, "end": v(-52.97, -73.83) * mm});
            skLineSegment(sketch, "E38.4.2.3", {"start": v(-48.34, -73.83) * mm, "end": v(-52.97, -73.83) * mm});
            skLineSegment(sketch, "E38.4.3.0", {"start": v(-48.34, -65.75) * mm, "end": v(-52.97, -65.75) * mm});
            skLineSegment(sketch, "E38.4.3.1", {"start": v(-48.34, -65.75) * mm, "end": v(-48.34, -61.13) * mm});
            skLineSegment(sketch, "E38.4.3.2", {"start": v(-52.97, -65.75) * mm, "end": v(-52.97, -61.13) * mm});
            skLineSegment(sketch, "E38.4.3.3", {"start": v(-48.34, -61.13) * mm, "end": v(-52.97, -61.13) * mm});
            skLineSegment(sketch, "E38.4.4.0", {"start": v(-48.34, -53.05) * mm, "end": v(-52.97, -53.05) * mm});
            skLineSegment(sketch, "E38.4.4.1", {"start": v(-48.34, -53.05) * mm, "end": v(-48.34, -48.43) * mm});
            skLineSegment(sketch, "E38.4.4.2", {"start": v(-52.97, -53.05) * mm, "end": v(-52.97, -48.43) * mm});
            skLineSegment(sketch, "E38.4.4.3", {"start": v(-48.34, -48.43) * mm, "end": v(-52.97, -48.43) * mm});
            skLineSegment(sketch, "E38.4.5.0", {"start": v(-48.34, -40.35) * mm, "end": v(-52.97, -40.35) * mm});
            skLineSegment(sketch, "E38.4.5.1", {"start": v(-48.34, -40.35) * mm, "end": v(-48.34, -35.73) * mm});
            skLineSegment(sketch, "E38.4.5.2", {"start": v(-52.97, -40.35) * mm, "end": v(-52.97, -35.73) * mm});
            skLineSegment(sketch, "E38.4.5.3", {"start": v(-48.34, -35.73) * mm, "end": v(-52.97, -35.73) * mm});
            skLineSegment(sketch, "E38.4.6.0", {"start": v(-48.34, -27.65) * mm, "end": v(-52.97, -27.65) * mm});
            skLineSegment(sketch, "E38.4.6.1", {"start": v(-48.34, -27.65) * mm, "end": v(-48.34, -23.03) * mm});
            skLineSegment(sketch, "E38.4.6.2", {"start": v(-52.97, -27.65) * mm, "end": v(-52.97, -23.03) * mm});
            skLineSegment(sketch, "E38.4.6.3", {"start": v(-48.34, -23.03) * mm, "end": v(-52.97, -23.03) * mm});
            skLineSegment(sketch, "E38.4.7.0", {"start": v(-48.34, -14.95) * mm, "end": v(-52.97, -14.95) * mm});
            skLineSegment(sketch, "E38.4.7.1", {"start": v(-48.34, -14.95) * mm, "end": v(-48.34, -10.33) * mm});
            skLineSegment(sketch, "E38.4.7.2", {"start": v(-52.97, -14.95) * mm, "end": v(-52.97, -10.33) * mm});
            skLineSegment(sketch, "E38.4.7.3", {"start": v(-48.34, -10.33) * mm, "end": v(-52.97, -10.33) * mm});
            skLineSegment(sketch, "E38.4.8.0", {"start": v(-48.34, -2.25) * mm, "end": v(-52.97, -2.25) * mm});
            skLineSegment(sketch, "E38.4.8.1", {"start": v(-48.34, -2.25) * mm, "end": v(-48.34, 2.37) * mm});
            skLineSegment(sketch, "E38.4.8.2", {"start": v(-52.97, -2.25) * mm, "end": v(-52.97, 2.37) * mm});
            skLineSegment(sketch, "E38.4.8.3", {"start": v(-48.34, 2.37) * mm, "end": v(-52.97, 2.37) * mm});
            skLineSegment(sketch, "E38.4.9.0", {"start": v(-48.34, 10.45) * mm, "end": v(-52.97, 10.45) * mm});
            skLineSegment(sketch, "E38.4.9.1", {"start": v(-48.34, 10.45) * mm, "end": v(-48.34, 15.07) * mm});
            skLineSegment(sketch, "E38.4.9.2", {"start": v(-52.97, 10.45) * mm, "end": v(-52.97, 15.07) * mm});
            skLineSegment(sketch, "E38.4.9.3", {"start": v(-48.34, 15.07) * mm, "end": v(-52.97, 15.07) * mm});
            skLineSegment(sketch, "E38.4.10.0", {"start": v(-48.34, 23.15) * mm, "end": v(-52.97, 23.15) * mm});
            skLineSegment(sketch, "E38.4.10.1", {"start": v(-48.34, 23.15) * mm, "end": v(-48.34, 27.77) * mm});
            skLineSegment(sketch, "E38.4.10.2", {"start": v(-52.97, 23.15) * mm, "end": v(-52.97, 27.77) * mm});
            skLineSegment(sketch, "E38.4.10.3", {"start": v(-48.34, 27.77) * mm, "end": v(-52.97, 27.77) * mm});
            skLineSegment(sketch, "E38.4.11.0", {"start": v(-48.34, 35.85) * mm, "end": v(-52.97, 35.85) * mm});
            skLineSegment(sketch, "E38.4.11.1", {"start": v(-48.34, 35.85) * mm, "end": v(-48.34, 40.47) * mm});
            skLineSegment(sketch, "E38.4.11.2", {"start": v(-52.97, 35.85) * mm, "end": v(-52.97, 40.47) * mm});
            skLineSegment(sketch, "E38.4.11.3", {"start": v(-48.34, 40.47) * mm, "end": v(-52.97, 40.47) * mm});
            skLineSegment(sketch, "E38.4.12.0", {"start": v(-48.34, 48.55) * mm, "end": v(-52.97, 48.55) * mm});
            skLineSegment(sketch, "E38.4.12.1", {"start": v(-48.34, 48.55) * mm, "end": v(-48.34, 53.17) * mm});
            skLineSegment(sketch, "E38.4.12.2", {"start": v(-52.97, 48.55) * mm, "end": v(-52.97, 53.17) * mm});
            skLineSegment(sketch, "E38.4.12.3", {"start": v(-48.34, 53.17) * mm, "end": v(-52.97, 53.17) * mm});
            skLineSegment(sketch, "E38.4.13.0", {"start": v(-48.34, 61.25) * mm, "end": v(-52.97, 61.25) * mm});
            skLineSegment(sketch, "E38.4.13.1", {"start": v(-48.34, 61.25) * mm, "end": v(-48.34, 65.87) * mm});
            skLineSegment(sketch, "E38.4.13.2", {"start": v(-52.97, 61.25) * mm, "end": v(-52.97, 65.87) * mm});
            skLineSegment(sketch, "E38.4.13.3", {"start": v(-48.34, 65.87) * mm, "end": v(-52.97, 65.87) * mm});
            skLineSegment(sketch, "E38.4.14.0", {"start": v(-48.34, 73.95) * mm, "end": v(-52.97, 73.95) * mm});
            skLineSegment(sketch, "E38.4.14.1", {"start": v(-48.34, 73.95) * mm, "end": v(-48.34, 78.57) * mm});
            skLineSegment(sketch, "E38.4.14.2", {"start": v(-52.97, 73.95) * mm, "end": v(-52.97, 78.57) * mm});
            skLineSegment(sketch, "E38.4.14.3", {"start": v(-48.34, 78.57) * mm, "end": v(-52.97, 78.57) * mm});
            skLineSegment(sketch, "E38.4.15.0", {"start": v(-48.34, 86.65) * mm, "end": v(-52.97, 86.65) * mm});
            skLineSegment(sketch, "E38.4.15.1", {"start": v(-48.34, 86.65) * mm, "end": v(-48.34, 91.27) * mm});
            skLineSegment(sketch, "E38.4.15.2", {"start": v(-52.97, 86.65) * mm, "end": v(-52.97, 91.27) * mm});
            skLineSegment(sketch, "E38.4.15.3", {"start": v(-48.34, 91.27) * mm, "end": v(-52.97, 91.27) * mm});
            skLineSegment(sketch, "E38.4.16.0", {"start": v(-48.34, 99.35) * mm, "end": v(-52.97, 99.35) * mm});
            skLineSegment(sketch, "E38.4.16.1", {"start": v(-48.34, 99.35) * mm, "end": v(-48.34, 103.97) * mm});
            skLineSegment(sketch, "E38.4.16.2", {"start": v(-52.97, 99.35) * mm, "end": v(-52.97, 103.97) * mm});
            skLineSegment(sketch, "E38.4.16.3", {"start": v(-48.34, 103.97) * mm, "end": v(-52.97, 103.97) * mm});
            skLineSegment(sketch, "E38.5.0.0", {"start": v(-35.64, -103.85) * mm, "end": v(-40.27, -103.85) * mm});
            skLineSegment(sketch, "E38.5.0.1", {"start": v(-35.64, -103.85) * mm, "end": v(-35.64, -99.23) * mm});
            skLineSegment(sketch, "E38.5.0.2", {"start": v(-40.27, -103.85) * mm, "end": v(-40.27, -99.23) * mm});
            skLineSegment(sketch, "E38.5.0.3", {"start": v(-35.64, -99.23) * mm, "end": v(-40.27, -99.23) * mm});
            skLineSegment(sketch, "E38.5.1.0", {"start": v(-35.64, -91.15) * mm, "end": v(-40.27, -91.15) * mm});
            skLineSegment(sketch, "E38.5.1.1", {"start": v(-35.64, -91.15) * mm, "end": v(-35.64, -86.53) * mm});
            skLineSegment(sketch, "E38.5.1.2", {"start": v(-40.27, -91.15) * mm, "end": v(-40.27, -86.53) * mm});
            skLineSegment(sketch, "E38.5.1.3", {"start": v(-35.64, -86.53) * mm, "end": v(-40.27, -86.53) * mm});
            skLineSegment(sketch, "E38.5.2.0", {"start": v(-35.64, -78.45) * mm, "end": v(-40.27, -78.45) * mm});
            skLineSegment(sketch, "E38.5.2.1", {"start": v(-35.64, -78.45) * mm, "end": v(-35.64, -73.83) * mm});
            skLineSegment(sketch, "E38.5.2.2", {"start": v(-40.27, -78.45) * mm, "end": v(-40.27, -73.83) * mm});
            skLineSegment(sketch, "E38.5.2.3", {"start": v(-35.64, -73.83) * mm, "end": v(-40.27, -73.83) * mm});
            skLineSegment(sketch, "E38.5.3.0", {"start": v(-35.64, -65.75) * mm, "end": v(-40.27, -65.75) * mm});
            skLineSegment(sketch, "E38.5.3.1", {"start": v(-35.64, -65.75) * mm, "end": v(-35.64, -61.13) * mm});
            skLineSegment(sketch, "E38.5.3.2", {"start": v(-40.27, -65.75) * mm, "end": v(-40.27, -61.13) * mm});
            skLineSegment(sketch, "E38.5.3.3", {"start": v(-35.64, -61.13) * mm, "end": v(-40.27, -61.13) * mm});
            skLineSegment(sketch, "E38.5.4.0", {"start": v(-35.64, -53.05) * mm, "end": v(-40.27, -53.05) * mm});
            skLineSegment(sketch, "E38.5.4.1", {"start": v(-35.64, -53.05) * mm, "end": v(-35.64, -48.43) * mm});
            skLineSegment(sketch, "E38.5.4.2", {"start": v(-40.27, -53.05) * mm, "end": v(-40.27, -48.43) * mm});
            skLineSegment(sketch, "E38.5.4.3", {"start": v(-35.64, -48.43) * mm, "end": v(-40.27, -48.43) * mm});
            skLineSegment(sketch, "E38.5.5.0", {"start": v(-35.64, -40.35) * mm, "end": v(-40.27, -40.35) * mm});
            skLineSegment(sketch, "E38.5.5.1", {"start": v(-35.64, -40.35) * mm, "end": v(-35.64, -35.73) * mm});
            skLineSegment(sketch, "E38.5.5.2", {"start": v(-40.27, -40.35) * mm, "end": v(-40.27, -35.73) * mm});
            skLineSegment(sketch, "E38.5.5.3", {"start": v(-35.64, -35.73) * mm, "end": v(-40.27, -35.73) * mm});
            skLineSegment(sketch, "E38.5.6.0", {"start": v(-35.64, -27.65) * mm, "end": v(-40.27, -27.65) * mm});
            skLineSegment(sketch, "E38.5.6.1", {"start": v(-35.64, -27.65) * mm, "end": v(-35.64, -23.03) * mm});
            skLineSegment(sketch, "E38.5.6.2", {"start": v(-40.27, -27.65) * mm, "end": v(-40.27, -23.03) * mm});
            skLineSegment(sketch, "E38.5.6.3", {"start": v(-35.64, -23.03) * mm, "end": v(-40.27, -23.03) * mm});
            skLineSegment(sketch, "E38.5.7.0", {"start": v(-35.64, -14.95) * mm, "end": v(-40.27, -14.95) * mm});
            skLineSegment(sketch, "E38.5.7.1", {"start": v(-35.64, -14.95) * mm, "end": v(-35.64, -10.33) * mm});
            skLineSegment(sketch, "E38.5.7.2", {"start": v(-40.27, -14.95) * mm, "end": v(-40.27, -10.33) * mm});
            skLineSegment(sketch, "E38.5.7.3", {"start": v(-35.64, -10.33) * mm, "end": v(-40.27, -10.33) * mm});
            skLineSegment(sketch, "E38.5.8.0", {"start": v(-35.64, -2.25) * mm, "end": v(-40.27, -2.25) * mm});
            skLineSegment(sketch, "E38.5.8.1", {"start": v(-35.64, -2.25) * mm, "end": v(-35.64, 2.37) * mm});
            skLineSegment(sketch, "E38.5.8.2", {"start": v(-40.27, -2.25) * mm, "end": v(-40.27, 2.37) * mm});
            skLineSegment(sketch, "E38.5.8.3", {"start": v(-35.64, 2.37) * mm, "end": v(-40.27, 2.37) * mm});
            skLineSegment(sketch, "E38.5.9.0", {"start": v(-35.64, 10.45) * mm, "end": v(-40.27, 10.45) * mm});
            skLineSegment(sketch, "E38.5.9.1", {"start": v(-35.64, 10.45) * mm, "end": v(-35.64, 15.07) * mm});
            skLineSegment(sketch, "E38.5.9.2", {"start": v(-40.27, 10.45) * mm, "end": v(-40.27, 15.07) * mm});
            skLineSegment(sketch, "E38.5.9.3", {"start": v(-35.64, 15.07) * mm, "end": v(-40.27, 15.07) * mm});
            skLineSegment(sketch, "E38.5.10.0", {"start": v(-35.64, 23.15) * mm, "end": v(-40.27, 23.15) * mm});
            skLineSegment(sketch, "E38.5.10.1", {"start": v(-35.64, 23.15) * mm, "end": v(-35.64, 27.77) * mm});
            skLineSegment(sketch, "E38.5.10.2", {"start": v(-40.27, 23.15) * mm, "end": v(-40.27, 27.77) * mm});
            skLineSegment(sketch, "E38.5.10.3", {"start": v(-35.64, 27.77) * mm, "end": v(-40.27, 27.77) * mm});
            skLineSegment(sketch, "E38.5.11.0", {"start": v(-35.64, 35.85) * mm, "end": v(-40.27, 35.85) * mm});
            skLineSegment(sketch, "E38.5.11.1", {"start": v(-35.64, 35.85) * mm, "end": v(-35.64, 40.47) * mm});
            skLineSegment(sketch, "E38.5.11.2", {"start": v(-40.27, 35.85) * mm, "end": v(-40.27, 40.47) * mm});
            skLineSegment(sketch, "E38.5.11.3", {"start": v(-35.64, 40.47) * mm, "end": v(-40.27, 40.47) * mm});
            skLineSegment(sketch, "E38.5.12.0", {"start": v(-35.64, 48.55) * mm, "end": v(-40.27, 48.55) * mm});
            skLineSegment(sketch, "E38.5.12.1", {"start": v(-35.64, 48.55) * mm, "end": v(-35.64, 53.17) * mm});
            skLineSegment(sketch, "E38.5.12.2", {"start": v(-40.27, 48.55) * mm, "end": v(-40.27, 53.17) * mm});
            skLineSegment(sketch, "E38.5.12.3", {"start": v(-35.64, 53.17) * mm, "end": v(-40.27, 53.17) * mm});
            skLineSegment(sketch, "E38.5.13.0", {"start": v(-35.64, 61.25) * mm, "end": v(-40.27, 61.25) * mm});
            skLineSegment(sketch, "E38.5.13.1", {"start": v(-35.64, 61.25) * mm, "end": v(-35.64, 65.87) * mm});
            skLineSegment(sketch, "E38.5.13.2", {"start": v(-40.27, 61.25) * mm, "end": v(-40.27, 65.87) * mm});
            skLineSegment(sketch, "E38.5.13.3", {"start": v(-35.64, 65.87) * mm, "end": v(-40.27, 65.87) * mm});
            skLineSegment(sketch, "E38.5.14.0", {"start": v(-35.64, 73.95) * mm, "end": v(-40.27, 73.95) * mm});
            skLineSegment(sketch, "E38.5.14.1", {"start": v(-35.64, 73.95) * mm, "end": v(-35.64, 78.57) * mm});
            skLineSegment(sketch, "E38.5.14.2", {"start": v(-40.27, 73.95) * mm, "end": v(-40.27, 78.57) * mm});
            skLineSegment(sketch, "E38.5.14.3", {"start": v(-35.64, 78.57) * mm, "end": v(-40.27, 78.57) * mm});
            skLineSegment(sketch, "E38.5.15.0", {"start": v(-35.64, 86.65) * mm, "end": v(-40.27, 86.65) * mm});
            skLineSegment(sketch, "E38.5.15.1", {"start": v(-35.64, 86.65) * mm, "end": v(-35.64, 91.27) * mm});
            skLineSegment(sketch, "E38.5.15.2", {"start": v(-40.27, 86.65) * mm, "end": v(-40.27, 91.27) * mm});
            skLineSegment(sketch, "E38.5.15.3", {"start": v(-35.64, 91.27) * mm, "end": v(-40.27, 91.27) * mm});
            skLineSegment(sketch, "E38.5.16.0", {"start": v(-35.64, 99.35) * mm, "end": v(-40.27, 99.35) * mm});
            skLineSegment(sketch, "E38.5.16.1", {"start": v(-35.64, 99.35) * mm, "end": v(-35.64, 103.97) * mm});
            skLineSegment(sketch, "E38.5.16.2", {"start": v(-40.27, 99.35) * mm, "end": v(-40.27, 103.97) * mm});
            skLineSegment(sketch, "E38.5.16.3", {"start": v(-35.64, 103.97) * mm, "end": v(-40.27, 103.97) * mm});
            skLineSegment(sketch, "E38.6.0.0", {"start": v(-22.94, -103.85) * mm, "end": v(-27.57, -103.85) * mm});
            skLineSegment(sketch, "E38.6.0.1", {"start": v(-22.94, -103.85) * mm, "end": v(-22.94, -99.23) * mm});
            skLineSegment(sketch, "E38.6.0.2", {"start": v(-27.57, -103.85) * mm, "end": v(-27.57, -99.23) * mm});
            skLineSegment(sketch, "E38.6.0.3", {"start": v(-22.94, -99.23) * mm, "end": v(-27.57, -99.23) * mm});
            skLineSegment(sketch, "E38.6.1.0", {"start": v(-22.94, -91.15) * mm, "end": v(-27.57, -91.15) * mm});
            skLineSegment(sketch, "E38.6.1.1", {"start": v(-22.94, -91.15) * mm, "end": v(-22.94, -86.53) * mm});
            skLineSegment(sketch, "E38.6.1.2", {"start": v(-27.57, -91.15) * mm, "end": v(-27.57, -86.53) * mm});
            skLineSegment(sketch, "E38.6.1.3", {"start": v(-22.94, -86.53) * mm, "end": v(-27.57, -86.53) * mm});
            skLineSegment(sketch, "E38.6.2.0", {"start": v(-22.94, -78.45) * mm, "end": v(-27.57, -78.45) * mm});
            skLineSegment(sketch, "E38.6.2.1", {"start": v(-22.94, -78.45) * mm, "end": v(-22.94, -73.83) * mm});
            skLineSegment(sketch, "E38.6.2.2", {"start": v(-27.57, -78.45) * mm, "end": v(-27.57, -73.83) * mm});
            skLineSegment(sketch, "E38.6.2.3", {"start": v(-22.94, -73.83) * mm, "end": v(-27.57, -73.83) * mm});
            skLineSegment(sketch, "E38.6.3.0", {"start": v(-22.94, -65.75) * mm, "end": v(-27.57, -65.75) * mm});
            skLineSegment(sketch, "E38.6.3.1", {"start": v(-22.94, -65.75) * mm, "end": v(-22.94, -61.13) * mm});
            skLineSegment(sketch, "E38.6.3.2", {"start": v(-27.57, -65.75) * mm, "end": v(-27.57, -61.13) * mm});
            skLineSegment(sketch, "E38.6.3.3", {"start": v(-22.94, -61.13) * mm, "end": v(-27.57, -61.13) * mm});
            skLineSegment(sketch, "E38.6.4.0", {"start": v(-22.94, -53.05) * mm, "end": v(-27.57, -53.05) * mm});
            skLineSegment(sketch, "E38.6.4.1", {"start": v(-22.94, -53.05) * mm, "end": v(-22.94, -48.43) * mm});
            skLineSegment(sketch, "E38.6.4.2", {"start": v(-27.57, -53.05) * mm, "end": v(-27.57, -48.43) * mm});
            skLineSegment(sketch, "E38.6.4.3", {"start": v(-22.94, -48.43) * mm, "end": v(-27.57, -48.43) * mm});
            skLineSegment(sketch, "E38.6.5.0", {"start": v(-22.94, -40.35) * mm, "end": v(-27.57, -40.35) * mm});
            skLineSegment(sketch, "E38.6.5.1", {"start": v(-22.94, -40.35) * mm, "end": v(-22.94, -35.73) * mm});
            skLineSegment(sketch, "E38.6.5.2", {"start": v(-27.57, -40.35) * mm, "end": v(-27.57, -35.73) * mm});
            skLineSegment(sketch, "E38.6.5.3", {"start": v(-22.94, -35.73) * mm, "end": v(-27.57, -35.73) * mm});
            skLineSegment(sketch, "E38.6.6.0", {"start": v(-22.94, -27.65) * mm, "end": v(-27.57, -27.65) * mm});
            skLineSegment(sketch, "E38.6.6.1", {"start": v(-22.94, -27.65) * mm, "end": v(-22.94, -23.03) * mm});
            skLineSegment(sketch, "E38.6.6.2", {"start": v(-27.57, -27.65) * mm, "end": v(-27.57, -23.03) * mm});
            skLineSegment(sketch, "E38.6.6.3", {"start": v(-22.94, -23.03) * mm, "end": v(-27.57, -23.03) * mm});
            skLineSegment(sketch, "E38.6.7.0", {"start": v(-22.94, -14.95) * mm, "end": v(-27.57, -14.95) * mm});
            skLineSegment(sketch, "E38.6.7.1", {"start": v(-22.94, -14.95) * mm, "end": v(-22.94, -10.33) * mm});
            skLineSegment(sketch, "E38.6.7.2", {"start": v(-27.57, -14.95) * mm, "end": v(-27.57, -10.33) * mm});
            skLineSegment(sketch, "E38.6.7.3", {"start": v(-22.94, -10.33) * mm, "end": v(-27.57, -10.33) * mm});
            skLineSegment(sketch, "E38.6.8.0", {"start": v(-22.94, -2.25) * mm, "end": v(-27.57, -2.25) * mm});
            skLineSegment(sketch, "E38.6.8.1", {"start": v(-22.94, -2.25) * mm, "end": v(-22.94, 2.37) * mm});
            skLineSegment(sketch, "E38.6.8.2", {"start": v(-27.57, -2.25) * mm, "end": v(-27.57, 2.37) * mm});
            skLineSegment(sketch, "E38.6.8.3", {"start": v(-22.94, 2.37) * mm, "end": v(-27.57, 2.37) * mm});
            skLineSegment(sketch, "E38.6.9.0", {"start": v(-22.94, 10.45) * mm, "end": v(-27.57, 10.45) * mm});
            skLineSegment(sketch, "E38.6.9.1", {"start": v(-22.94, 10.45) * mm, "end": v(-22.94, 15.07) * mm});
            skLineSegment(sketch, "E38.6.9.2", {"start": v(-27.57, 10.45) * mm, "end": v(-27.57, 15.07) * mm});
            skLineSegment(sketch, "E38.6.9.3", {"start": v(-22.94, 15.07) * mm, "end": v(-27.57, 15.07) * mm});
            skLineSegment(sketch, "E38.6.10.0", {"start": v(-22.94, 23.15) * mm, "end": v(-27.57, 23.15) * mm});
            skLineSegment(sketch, "E38.6.10.1", {"start": v(-22.94, 23.15) * mm, "end": v(-22.94, 27.77) * mm});
            skLineSegment(sketch, "E38.6.10.2", {"start": v(-27.57, 23.15) * mm, "end": v(-27.57, 27.77) * mm});
            skLineSegment(sketch, "E38.6.10.3", {"start": v(-22.94, 27.77) * mm, "end": v(-27.57, 27.77) * mm});
            skLineSegment(sketch, "E38.6.11.0", {"start": v(-22.94, 35.85) * mm, "end": v(-27.57, 35.85) * mm});
            skLineSegment(sketch, "E38.6.11.1", {"start": v(-22.94, 35.85) * mm, "end": v(-22.94, 40.47) * mm});
            skLineSegment(sketch, "E38.6.11.2", {"start": v(-27.57, 35.85) * mm, "end": v(-27.57, 40.47) * mm});
            skLineSegment(sketch, "E38.6.11.3", {"start": v(-22.94, 40.47) * mm, "end": v(-27.57, 40.47) * mm});
            skLineSegment(sketch, "E38.6.12.0", {"start": v(-22.94, 48.55) * mm, "end": v(-27.57, 48.55) * mm});
            skLineSegment(sketch, "E38.6.12.1", {"start": v(-22.94, 48.55) * mm, "end": v(-22.94, 53.17) * mm});
            skLineSegment(sketch, "E38.6.12.2", {"start": v(-27.57, 48.55) * mm, "end": v(-27.57, 53.17) * mm});
            skLineSegment(sketch, "E38.6.12.3", {"start": v(-22.94, 53.17) * mm, "end": v(-27.57, 53.17) * mm});
            skLineSegment(sketch, "E38.6.13.0", {"start": v(-22.94, 61.25) * mm, "end": v(-27.57, 61.25) * mm});
            skLineSegment(sketch, "E38.6.13.1", {"start": v(-22.94, 61.25) * mm, "end": v(-22.94, 65.87) * mm});
            skLineSegment(sketch, "E38.6.13.2", {"start": v(-27.57, 61.25) * mm, "end": v(-27.57, 65.87) * mm});
            skLineSegment(sketch, "E38.6.13.3", {"start": v(-22.94, 65.87) * mm, "end": v(-27.57, 65.87) * mm});
            skLineSegment(sketch, "E38.6.14.0", {"start": v(-22.94, 73.95) * mm, "end": v(-27.57, 73.95) * mm});
            skLineSegment(sketch, "E38.6.14.1", {"start": v(-22.94, 73.95) * mm, "end": v(-22.94, 78.57) * mm});
            skLineSegment(sketch, "E38.6.14.2", {"start": v(-27.57, 73.95) * mm, "end": v(-27.57, 78.57) * mm});
            skLineSegment(sketch, "E38.6.14.3", {"start": v(-22.94, 78.57) * mm, "end": v(-27.57, 78.57) * mm});
            skLineSegment(sketch, "E38.6.15.0", {"start": v(-22.94, 86.65) * mm, "end": v(-27.57, 86.65) * mm});
            skLineSegment(sketch, "E38.6.15.1", {"start": v(-22.94, 86.65) * mm, "end": v(-22.94, 91.27) * mm});
            skLineSegment(sketch, "E38.6.15.2", {"start": v(-27.57, 86.65) * mm, "end": v(-27.57, 91.27) * mm});
            skLineSegment(sketch, "E38.6.15.3", {"start": v(-22.94, 91.27) * mm, "end": v(-27.57, 91.27) * mm});
            skLineSegment(sketch, "E38.6.16.0", {"start": v(-22.94, 99.35) * mm, "end": v(-27.57, 99.35) * mm});
            skLineSegment(sketch, "E38.6.16.1", {"start": v(-22.94, 99.35) * mm, "end": v(-22.94, 103.97) * mm});
            skLineSegment(sketch, "E38.6.16.2", {"start": v(-27.57, 99.35) * mm, "end": v(-27.57, 103.97) * mm});
            skLineSegment(sketch, "E38.6.16.3", {"start": v(-22.94, 103.97) * mm, "end": v(-27.57, 103.97) * mm});
            skLineSegment(sketch, "E38.7.0.0", {"start": v(-10.24, -103.85) * mm, "end": v(-14.87, -103.85) * mm});
            skLineSegment(sketch, "E38.7.0.1", {"start": v(-10.24, -103.85) * mm, "end": v(-10.24, -99.23) * mm});
            skLineSegment(sketch, "E38.7.0.2", {"start": v(-14.87, -103.85) * mm, "end": v(-14.87, -99.23) * mm});
            skLineSegment(sketch, "E38.7.0.3", {"start": v(-10.24, -99.23) * mm, "end": v(-14.87, -99.23) * mm});
            skLineSegment(sketch, "E38.7.1.0", {"start": v(-10.24, -91.15) * mm, "end": v(-14.87, -91.15) * mm});
            skLineSegment(sketch, "E38.7.1.1", {"start": v(-10.24, -91.15) * mm, "end": v(-10.24, -86.53) * mm});
            skLineSegment(sketch, "E38.7.1.2", {"start": v(-14.87, -91.15) * mm, "end": v(-14.87, -86.53) * mm});
            skLineSegment(sketch, "E38.7.1.3", {"start": v(-10.24, -86.53) * mm, "end": v(-14.87, -86.53) * mm});
            skLineSegment(sketch, "E38.7.2.0", {"start": v(-10.24, -78.45) * mm, "end": v(-14.87, -78.45) * mm});
            skLineSegment(sketch, "E38.7.2.1", {"start": v(-10.24, -78.45) * mm, "end": v(-10.24, -73.83) * mm});
            skLineSegment(sketch, "E38.7.2.2", {"start": v(-14.87, -78.45) * mm, "end": v(-14.87, -73.83) * mm});
            skLineSegment(sketch, "E38.7.2.3", {"start": v(-10.24, -73.83) * mm, "end": v(-14.87, -73.83) * mm});
            skLineSegment(sketch, "E38.7.3.0", {"start": v(-10.24, -65.75) * mm, "end": v(-14.87, -65.75) * mm});
            skLineSegment(sketch, "E38.7.3.1", {"start": v(-10.24, -65.75) * mm, "end": v(-10.24, -61.13) * mm});
            skLineSegment(sketch, "E38.7.3.2", {"start": v(-14.87, -65.75) * mm, "end": v(-14.87, -61.13) * mm});
            skLineSegment(sketch, "E38.7.3.3", {"start": v(-10.24, -61.13) * mm, "end": v(-14.87, -61.13) * mm});
            skLineSegment(sketch, "E38.7.4.0", {"start": v(-10.24, -53.05) * mm, "end": v(-14.87, -53.05) * mm});
            skLineSegment(sketch, "E38.7.4.1", {"start": v(-10.24, -53.05) * mm, "end": v(-10.24, -48.43) * mm});
            skLineSegment(sketch, "E38.7.4.2", {"start": v(-14.87, -53.05) * mm, "end": v(-14.87, -48.43) * mm});
            skLineSegment(sketch, "E38.7.4.3", {"start": v(-10.24, -48.43) * mm, "end": v(-14.87, -48.43) * mm});
            skLineSegment(sketch, "E38.7.5.0", {"start": v(-10.24, -40.35) * mm, "end": v(-14.87, -40.35) * mm});
            skLineSegment(sketch, "E38.7.5.1", {"start": v(-10.24, -40.35) * mm, "end": v(-10.24, -35.73) * mm});
            skLineSegment(sketch, "E38.7.5.2", {"start": v(-14.87, -40.35) * mm, "end": v(-14.87, -35.73) * mm});
            skLineSegment(sketch, "E38.7.5.3", {"start": v(-10.24, -35.73) * mm, "end": v(-14.87, -35.73) * mm});
            skLineSegment(sketch, "E38.7.6.0", {"start": v(-10.24, -27.65) * mm, "end": v(-14.87, -27.65) * mm});
            skLineSegment(sketch, "E38.7.6.1", {"start": v(-10.24, -27.65) * mm, "end": v(-10.24, -23.03) * mm});
            skLineSegment(sketch, "E38.7.6.2", {"start": v(-14.87, -27.65) * mm, "end": v(-14.87, -23.03) * mm});
            skLineSegment(sketch, "E38.7.6.3", {"start": v(-10.24, -23.03) * mm, "end": v(-14.87, -23.03) * mm});
            skLineSegment(sketch, "E38.7.7.0", {"start": v(-10.24, -14.95) * mm, "end": v(-14.87, -14.95) * mm});
            skLineSegment(sketch, "E38.7.7.1", {"start": v(-10.24, -14.95) * mm, "end": v(-10.24, -10.33) * mm});
            skLineSegment(sketch, "E38.7.7.2", {"start": v(-14.87, -14.95) * mm, "end": v(-14.87, -10.33) * mm});
            skLineSegment(sketch, "E38.7.7.3", {"start": v(-10.24, -10.33) * mm, "end": v(-14.87, -10.33) * mm});
            skLineSegment(sketch, "E38.7.8.0", {"start": v(-10.24, -2.25) * mm, "end": v(-14.87, -2.25) * mm});
            skLineSegment(sketch, "E38.7.8.1", {"start": v(-10.24, -2.25) * mm, "end": v(-10.24, 2.37) * mm});
            skLineSegment(sketch, "E38.7.8.2", {"start": v(-14.87, -2.25) * mm, "end": v(-14.87, 2.37) * mm});
            skLineSegment(sketch, "E38.7.8.3", {"start": v(-10.24, 2.37) * mm, "end": v(-14.87, 2.37) * mm});
            skLineSegment(sketch, "E38.7.9.0", {"start": v(-10.24, 10.45) * mm, "end": v(-14.87, 10.45) * mm});
            skLineSegment(sketch, "E38.7.9.1", {"start": v(-10.24, 10.45) * mm, "end": v(-10.24, 15.07) * mm});
            skLineSegment(sketch, "E38.7.9.2", {"start": v(-14.87, 10.45) * mm, "end": v(-14.87, 15.07) * mm});
            skLineSegment(sketch, "E38.7.9.3", {"start": v(-10.24, 15.07) * mm, "end": v(-14.87, 15.07) * mm});
            skLineSegment(sketch, "E38.7.10.0", {"start": v(-10.24, 23.15) * mm, "end": v(-14.87, 23.15) * mm});
            skLineSegment(sketch, "E38.7.10.1", {"start": v(-10.24, 23.15) * mm, "end": v(-10.24, 27.77) * mm});
            skLineSegment(sketch, "E38.7.10.2", {"start": v(-14.87, 23.15) * mm, "end": v(-14.87, 27.77) * mm});
            skLineSegment(sketch, "E38.7.10.3", {"start": v(-10.24, 27.77) * mm, "end": v(-14.87, 27.77) * mm});
            skLineSegment(sketch, "E38.7.11.0", {"start": v(-10.24, 35.85) * mm, "end": v(-14.87, 35.85) * mm});
            skLineSegment(sketch, "E38.7.11.1", {"start": v(-10.24, 35.85) * mm, "end": v(-10.24, 40.47) * mm});
            skLineSegment(sketch, "E38.7.11.2", {"start": v(-14.87, 35.85) * mm, "end": v(-14.87, 40.47) * mm});
            skLineSegment(sketch, "E38.7.11.3", {"start": v(-10.24, 40.47) * mm, "end": v(-14.87, 40.47) * mm});
            skLineSegment(sketch, "E38.7.12.0", {"start": v(-10.24, 48.55) * mm, "end": v(-14.87, 48.55) * mm});
            skLineSegment(sketch, "E38.7.12.1", {"start": v(-10.24, 48.55) * mm, "end": v(-10.24, 53.17) * mm});
            skLineSegment(sketch, "E38.7.12.2", {"start": v(-14.87, 48.55) * mm, "end": v(-14.87, 53.17) * mm});
            skLineSegment(sketch, "E38.7.12.3", {"start": v(-10.24, 53.17) * mm, "end": v(-14.87, 53.17) * mm});
            skLineSegment(sketch, "E38.7.13.0", {"start": v(-10.24, 61.25) * mm, "end": v(-14.87, 61.25) * mm});
            skLineSegment(sketch, "E38.7.13.1", {"start": v(-10.24, 61.25) * mm, "end": v(-10.24, 65.87) * mm});
            skLineSegment(sketch, "E38.7.13.2", {"start": v(-14.87, 61.25) * mm, "end": v(-14.87, 65.87) * mm});
            skLineSegment(sketch, "E38.7.13.3", {"start": v(-10.24, 65.87) * mm, "end": v(-14.87, 65.87) * mm});
            skLineSegment(sketch, "E38.7.14.0", {"start": v(-10.24, 73.95) * mm, "end": v(-14.87, 73.95) * mm});
            skLineSegment(sketch, "E38.7.14.1", {"start": v(-10.24, 73.95) * mm, "end": v(-10.24, 78.57) * mm});
            skLineSegment(sketch, "E38.7.14.2", {"start": v(-14.87, 73.95) * mm, "end": v(-14.87, 78.57) * mm});
            skLineSegment(sketch, "E38.7.14.3", {"start": v(-10.24, 78.57) * mm, "end": v(-14.87, 78.57) * mm});
            skLineSegment(sketch, "E38.7.15.0", {"start": v(-10.24, 86.65) * mm, "end": v(-14.87, 86.65) * mm});
            skLineSegment(sketch, "E38.7.15.1", {"start": v(-10.24, 86.65) * mm, "end": v(-10.24, 91.27) * mm});
            skLineSegment(sketch, "E38.7.15.2", {"start": v(-14.87, 86.65) * mm, "end": v(-14.87, 91.27) * mm});
            skLineSegment(sketch, "E38.7.15.3", {"start": v(-10.24, 91.27) * mm, "end": v(-14.87, 91.27) * mm});
            skLineSegment(sketch, "E38.7.16.0", {"start": v(-10.24, 99.35) * mm, "end": v(-14.87, 99.35) * mm});
            skLineSegment(sketch, "E38.7.16.1", {"start": v(-10.24, 99.35) * mm, "end": v(-10.24, 103.97) * mm});
            skLineSegment(sketch, "E38.7.16.2", {"start": v(-14.87, 99.35) * mm, "end": v(-14.87, 103.97) * mm});
            skLineSegment(sketch, "E38.7.16.3", {"start": v(-10.24, 103.97) * mm, "end": v(-14.87, 103.97) * mm});
            skLineSegment(sketch, "E38.8.0.0", {"start": v(2.46, -103.85) * mm, "end": v(-2.17, -103.85) * mm});
            skLineSegment(sketch, "E38.8.0.1", {"start": v(2.46, -103.85) * mm, "end": v(2.46, -99.23) * mm});
            skLineSegment(sketch, "E38.8.0.2", {"start": v(-2.17, -103.85) * mm, "end": v(-2.17, -99.23) * mm});
            skLineSegment(sketch, "E38.8.0.3", {"start": v(2.46, -99.23) * mm, "end": v(-2.17, -99.23) * mm});
            skLineSegment(sketch, "E38.8.1.0", {"start": v(2.46, -91.15) * mm, "end": v(-2.17, -91.15) * mm});
            skLineSegment(sketch, "E38.8.1.1", {"start": v(2.46, -91.15) * mm, "end": v(2.46, -86.53) * mm});
            skLineSegment(sketch, "E38.8.1.2", {"start": v(-2.17, -91.15) * mm, "end": v(-2.17, -86.53) * mm});
            skLineSegment(sketch, "E38.8.1.3", {"start": v(2.46, -86.53) * mm, "end": v(-2.17, -86.53) * mm});
            skLineSegment(sketch, "E38.8.2.0", {"start": v(2.46, -78.45) * mm, "end": v(-2.17, -78.45) * mm});
            skLineSegment(sketch, "E38.8.2.1", {"start": v(2.46, -78.45) * mm, "end": v(2.46, -73.83) * mm});
            skLineSegment(sketch, "E38.8.2.2", {"start": v(-2.17, -78.45) * mm, "end": v(-2.17, -73.83) * mm});
            skLineSegment(sketch, "E38.8.2.3", {"start": v(2.46, -73.83) * mm, "end": v(-2.17, -73.83) * mm});
            skLineSegment(sketch, "E38.8.3.0", {"start": v(2.46, -65.75) * mm, "end": v(-2.17, -65.75) * mm});
            skLineSegment(sketch, "E38.8.3.1", {"start": v(2.46, -65.75) * mm, "end": v(2.46, -61.13) * mm});
            skLineSegment(sketch, "E38.8.3.2", {"start": v(-2.17, -65.75) * mm, "end": v(-2.17, -61.13) * mm});
            skLineSegment(sketch, "E38.8.3.3", {"start": v(2.46, -61.13) * mm, "end": v(-2.17, -61.13) * mm});
            skLineSegment(sketch, "E38.8.4.0", {"start": v(2.46, -53.05) * mm, "end": v(-2.17, -53.05) * mm});
            skLineSegment(sketch, "E38.8.4.1", {"start": v(2.46, -53.05) * mm, "end": v(2.46, -48.43) * mm});
            skLineSegment(sketch, "E38.8.4.2", {"start": v(-2.17, -53.05) * mm, "end": v(-2.17, -48.43) * mm});
            skLineSegment(sketch, "E38.8.4.3", {"start": v(2.46, -48.43) * mm, "end": v(-2.17, -48.43) * mm});
            skLineSegment(sketch, "E38.8.5.0", {"start": v(2.46, -40.35) * mm, "end": v(-2.17, -40.35) * mm});
            skLineSegment(sketch, "E38.8.5.1", {"start": v(2.46, -40.35) * mm, "end": v(2.46, -35.73) * mm});
            skLineSegment(sketch, "E38.8.5.2", {"start": v(-2.17, -40.35) * mm, "end": v(-2.17, -35.73) * mm});
            skLineSegment(sketch, "E38.8.5.3", {"start": v(2.46, -35.73) * mm, "end": v(-2.17, -35.73) * mm});
            skLineSegment(sketch, "E38.8.6.0", {"start": v(2.46, -27.65) * mm, "end": v(-2.17, -27.65) * mm});
            skLineSegment(sketch, "E38.8.6.1", {"start": v(2.46, -27.65) * mm, "end": v(2.46, -23.03) * mm});
            skLineSegment(sketch, "E38.8.6.2", {"start": v(-2.17, -27.65) * mm, "end": v(-2.17, -23.03) * mm});
            skLineSegment(sketch, "E38.8.6.3", {"start": v(2.46, -23.03) * mm, "end": v(-2.17, -23.03) * mm});
            skLineSegment(sketch, "E38.8.7.0", {"start": v(2.46, -14.95) * mm, "end": v(-2.17, -14.95) * mm});
            skLineSegment(sketch, "E38.8.7.1", {"start": v(2.46, -14.95) * mm, "end": v(2.46, -10.33) * mm});
            skLineSegment(sketch, "E38.8.7.2", {"start": v(-2.17, -14.95) * mm, "end": v(-2.17, -10.33) * mm});
            skLineSegment(sketch, "E38.8.7.3", {"start": v(2.46, -10.33) * mm, "end": v(-2.17, -10.33) * mm});
            skLineSegment(sketch, "E38.8.8.0", {"start": v(2.46, -2.25) * mm, "end": v(-2.17, -2.25) * mm});
            skLineSegment(sketch, "E38.8.8.1", {"start": v(2.46, -2.25) * mm, "end": v(2.46, 2.37) * mm});
            skLineSegment(sketch, "E38.8.8.2", {"start": v(-2.17, -2.25) * mm, "end": v(-2.17, 2.37) * mm});
            skLineSegment(sketch, "E38.8.8.3", {"start": v(2.46, 2.37) * mm, "end": v(-2.17, 2.37) * mm});
            skLineSegment(sketch, "E38.8.9.0", {"start": v(2.46, 10.45) * mm, "end": v(-2.17, 10.45) * mm});
            skLineSegment(sketch, "E38.8.9.1", {"start": v(2.46, 10.45) * mm, "end": v(2.46, 15.07) * mm});
            skLineSegment(sketch, "E38.8.9.2", {"start": v(-2.17, 10.45) * mm, "end": v(-2.17, 15.07) * mm});
            skLineSegment(sketch, "E38.8.9.3", {"start": v(2.46, 15.07) * mm, "end": v(-2.17, 15.07) * mm});
            skLineSegment(sketch, "E38.8.10.0", {"start": v(2.46, 23.15) * mm, "end": v(-2.17, 23.15) * mm});
            skLineSegment(sketch, "E38.8.10.1", {"start": v(2.46, 23.15) * mm, "end": v(2.46, 27.77) * mm});
            skLineSegment(sketch, "E38.8.10.2", {"start": v(-2.17, 23.15) * mm, "end": v(-2.17, 27.77) * mm});
            skLineSegment(sketch, "E38.8.10.3", {"start": v(2.46, 27.77) * mm, "end": v(-2.17, 27.77) * mm});
            skLineSegment(sketch, "E38.8.11.0", {"start": v(2.46, 35.85) * mm, "end": v(-2.17, 35.85) * mm});
            skLineSegment(sketch, "E38.8.11.1", {"start": v(2.46, 35.85) * mm, "end": v(2.46, 40.47) * mm});
            skLineSegment(sketch, "E38.8.11.2", {"start": v(-2.17, 35.85) * mm, "end": v(-2.17, 40.47) * mm});
            skLineSegment(sketch, "E38.8.11.3", {"start": v(2.46, 40.47) * mm, "end": v(-2.17, 40.47) * mm});
            skLineSegment(sketch, "E38.8.12.0", {"start": v(2.46, 48.55) * mm, "end": v(-2.17, 48.55) * mm});
            skLineSegment(sketch, "E38.8.12.1", {"start": v(2.46, 48.55) * mm, "end": v(2.46, 53.17) * mm});
            skLineSegment(sketch, "E38.8.12.2", {"start": v(-2.17, 48.55) * mm, "end": v(-2.17, 53.17) * mm});
            skLineSegment(sketch, "E38.8.12.3", {"start": v(2.46, 53.17) * mm, "end": v(-2.17, 53.17) * mm});
            skLineSegment(sketch, "E38.8.13.0", {"start": v(2.46, 61.25) * mm, "end": v(-2.17, 61.25) * mm});
            skLineSegment(sketch, "E38.8.13.1", {"start": v(2.46, 61.25) * mm, "end": v(2.46, 65.87) * mm});
            skLineSegment(sketch, "E38.8.13.2", {"start": v(-2.17, 61.25) * mm, "end": v(-2.17, 65.87) * mm});
            skLineSegment(sketch, "E38.8.13.3", {"start": v(2.46, 65.87) * mm, "end": v(-2.17, 65.87) * mm});
            skLineSegment(sketch, "E38.8.14.0", {"start": v(2.46, 73.95) * mm, "end": v(-2.17, 73.95) * mm});
            skLineSegment(sketch, "E38.8.14.1", {"start": v(2.46, 73.95) * mm, "end": v(2.46, 78.57) * mm});
            skLineSegment(sketch, "E38.8.14.2", {"start": v(-2.17, 73.95) * mm, "end": v(-2.17, 78.57) * mm});
            skLineSegment(sketch, "E38.8.14.3", {"start": v(2.46, 78.57) * mm, "end": v(-2.17, 78.57) * mm});
            skLineSegment(sketch, "E38.8.15.0", {"start": v(2.46, 86.65) * mm, "end": v(-2.17, 86.65) * mm});
            skLineSegment(sketch, "E38.8.15.1", {"start": v(2.46, 86.65) * mm, "end": v(2.46, 91.27) * mm});
            skLineSegment(sketch, "E38.8.15.2", {"start": v(-2.17, 86.65) * mm, "end": v(-2.17, 91.27) * mm});
            skLineSegment(sketch, "E38.8.15.3", {"start": v(2.46, 91.27) * mm, "end": v(-2.17, 91.27) * mm});
            skLineSegment(sketch, "E38.8.16.0", {"start": v(2.46, 99.35) * mm, "end": v(-2.17, 99.35) * mm});
            skLineSegment(sketch, "E38.8.16.1", {"start": v(2.46, 99.35) * mm, "end": v(2.46, 103.97) * mm});
            skLineSegment(sketch, "E38.8.16.2", {"start": v(-2.17, 99.35) * mm, "end": v(-2.17, 103.97) * mm});
            skLineSegment(sketch, "E38.8.16.3", {"start": v(2.46, 103.97) * mm, "end": v(-2.17, 103.97) * mm});
            skLineSegment(sketch, "E38.9.0.0", {"start": v(15.16, -103.85) * mm, "end": v(10.53, -103.85) * mm});
            skLineSegment(sketch, "E38.9.0.1", {"start": v(15.16, -103.85) * mm, "end": v(15.16, -99.23) * mm});
            skLineSegment(sketch, "E38.9.0.2", {"start": v(10.53, -103.85) * mm, "end": v(10.53, -99.23) * mm});
            skLineSegment(sketch, "E38.9.0.3", {"start": v(15.16, -99.23) * mm, "end": v(10.53, -99.23) * mm});
            skLineSegment(sketch, "E38.9.1.0", {"start": v(15.16, -91.15) * mm, "end": v(10.53, -91.15) * mm});
            skLineSegment(sketch, "E38.9.1.1", {"start": v(15.16, -91.15) * mm, "end": v(15.16, -86.53) * mm});
            skLineSegment(sketch, "E38.9.1.2", {"start": v(10.53, -91.15) * mm, "end": v(10.53, -86.53) * mm});
            skLineSegment(sketch, "E38.9.1.3", {"start": v(15.16, -86.53) * mm, "end": v(10.53, -86.53) * mm});
            skLineSegment(sketch, "E38.9.2.0", {"start": v(15.16, -78.45) * mm, "end": v(10.53, -78.45) * mm});
            skLineSegment(sketch, "E38.9.2.1", {"start": v(15.16, -78.45) * mm, "end": v(15.16, -73.83) * mm});
            skLineSegment(sketch, "E38.9.2.2", {"start": v(10.53, -78.45) * mm, "end": v(10.53, -73.83) * mm});
            skLineSegment(sketch, "E38.9.2.3", {"start": v(15.16, -73.83) * mm, "end": v(10.53, -73.83) * mm});
            skLineSegment(sketch, "E38.9.3.0", {"start": v(15.16, -65.75) * mm, "end": v(10.53, -65.75) * mm});
            skLineSegment(sketch, "E38.9.3.1", {"start": v(15.16, -65.75) * mm, "end": v(15.16, -61.13) * mm});
            skLineSegment(sketch, "E38.9.3.2", {"start": v(10.53, -65.75) * mm, "end": v(10.53, -61.13) * mm});
            skLineSegment(sketch, "E38.9.3.3", {"start": v(15.16, -61.13) * mm, "end": v(10.53, -61.13) * mm});
            skLineSegment(sketch, "E38.9.4.0", {"start": v(15.16, -53.05) * mm, "end": v(10.53, -53.05) * mm});
            skLineSegment(sketch, "E38.9.4.1", {"start": v(15.16, -53.05) * mm, "end": v(15.16, -48.43) * mm});
            skLineSegment(sketch, "E38.9.4.2", {"start": v(10.53, -53.05) * mm, "end": v(10.53, -48.43) * mm});
            skLineSegment(sketch, "E38.9.4.3", {"start": v(15.16, -48.43) * mm, "end": v(10.53, -48.43) * mm});
            skLineSegment(sketch, "E38.9.5.0", {"start": v(15.16, -40.35) * mm, "end": v(10.53, -40.35) * mm});
            skLineSegment(sketch, "E38.9.5.1", {"start": v(15.16, -40.35) * mm, "end": v(15.16, -35.73) * mm});
            skLineSegment(sketch, "E38.9.5.2", {"start": v(10.53, -40.35) * mm, "end": v(10.53, -35.73) * mm});
            skLineSegment(sketch, "E38.9.5.3", {"start": v(15.16, -35.73) * mm, "end": v(10.53, -35.73) * mm});
            skLineSegment(sketch, "E38.9.6.0", {"start": v(15.16, -27.65) * mm, "end": v(10.53, -27.65) * mm});
            skLineSegment(sketch, "E38.9.6.1", {"start": v(15.16, -27.65) * mm, "end": v(15.16, -23.03) * mm});
            skLineSegment(sketch, "E38.9.6.2", {"start": v(10.53, -27.65) * mm, "end": v(10.53, -23.03) * mm});
            skLineSegment(sketch, "E38.9.6.3", {"start": v(15.16, -23.03) * mm, "end": v(10.53, -23.03) * mm});
            skLineSegment(sketch, "E38.9.7.0", {"start": v(15.16, -14.95) * mm, "end": v(10.53, -14.95) * mm});
            skLineSegment(sketch, "E38.9.7.1", {"start": v(15.16, -14.95) * mm, "end": v(15.16, -10.33) * mm});
            skLineSegment(sketch, "E38.9.7.2", {"start": v(10.53, -14.95) * mm, "end": v(10.53, -10.33) * mm});
            skLineSegment(sketch, "E38.9.7.3", {"start": v(15.16, -10.33) * mm, "end": v(10.53, -10.33) * mm});
            skLineSegment(sketch, "E38.9.8.0", {"start": v(15.16, -2.25) * mm, "end": v(10.53, -2.25) * mm});
            skLineSegment(sketch, "E38.9.8.1", {"start": v(15.16, -2.25) * mm, "end": v(15.16, 2.37) * mm});
            skLineSegment(sketch, "E38.9.8.2", {"start": v(10.53, -2.25) * mm, "end": v(10.53, 2.37) * mm});
            skLineSegment(sketch, "E38.9.8.3", {"start": v(15.16, 2.37) * mm, "end": v(10.53, 2.37) * mm});
            skLineSegment(sketch, "E38.9.9.0", {"start": v(15.16, 10.45) * mm, "end": v(10.53, 10.45) * mm});
            skLineSegment(sketch, "E38.9.9.1", {"start": v(15.16, 10.45) * mm, "end": v(15.16, 15.07) * mm});
            skLineSegment(sketch, "E38.9.9.2", {"start": v(10.53, 10.45) * mm, "end": v(10.53, 15.07) * mm});
            skLineSegment(sketch, "E38.9.9.3", {"start": v(15.16, 15.07) * mm, "end": v(10.53, 15.07) * mm});
            skLineSegment(sketch, "E38.9.10.0", {"start": v(15.16, 23.15) * mm, "end": v(10.53, 23.15) * mm});
            skLineSegment(sketch, "E38.9.10.1", {"start": v(15.16, 23.15) * mm, "end": v(15.16, 27.77) * mm});
            skLineSegment(sketch, "E38.9.10.2", {"start": v(10.53, 23.15) * mm, "end": v(10.53, 27.77) * mm});
            skLineSegment(sketch, "E38.9.10.3", {"start": v(15.16, 27.77) * mm, "end": v(10.53, 27.77) * mm});
            skLineSegment(sketch, "E38.9.11.0", {"start": v(15.16, 35.85) * mm, "end": v(10.53, 35.85) * mm});
            skLineSegment(sketch, "E38.9.11.1", {"start": v(15.16, 35.85) * mm, "end": v(15.16, 40.47) * mm});
            skLineSegment(sketch, "E38.9.11.2", {"start": v(10.53, 35.85) * mm, "end": v(10.53, 40.47) * mm});
            skLineSegment(sketch, "E38.9.11.3", {"start": v(15.16, 40.47) * mm, "end": v(10.53, 40.47) * mm});
            skLineSegment(sketch, "E38.9.12.0", {"start": v(15.16, 48.55) * mm, "end": v(10.53, 48.55) * mm});
            skLineSegment(sketch, "E38.9.12.1", {"start": v(15.16, 48.55) * mm, "end": v(15.16, 53.17) * mm});
            skLineSegment(sketch, "E38.9.12.2", {"start": v(10.53, 48.55) * mm, "end": v(10.53, 53.17) * mm});
            skLineSegment(sketch, "E38.9.12.3", {"start": v(15.16, 53.17) * mm, "end": v(10.53, 53.17) * mm});
            skLineSegment(sketch, "E38.9.13.0", {"start": v(15.16, 61.25) * mm, "end": v(10.53, 61.25) * mm});
            skLineSegment(sketch, "E38.9.13.1", {"start": v(15.16, 61.25) * mm, "end": v(15.16, 65.87) * mm});
            skLineSegment(sketch, "E38.9.13.2", {"start": v(10.53, 61.25) * mm, "end": v(10.53, 65.87) * mm});
            skLineSegment(sketch, "E38.9.13.3", {"start": v(15.16, 65.87) * mm, "end": v(10.53, 65.87) * mm});
            skLineSegment(sketch, "E38.9.14.0", {"start": v(15.16, 73.95) * mm, "end": v(10.53, 73.95) * mm});
            skLineSegment(sketch, "E38.9.14.1", {"start": v(15.16, 73.95) * mm, "end": v(15.16, 78.57) * mm});
            skLineSegment(sketch, "E38.9.14.2", {"start": v(10.53, 73.95) * mm, "end": v(10.53, 78.57) * mm});
            skLineSegment(sketch, "E38.9.14.3", {"start": v(15.16, 78.57) * mm, "end": v(10.53, 78.57) * mm});
            skLineSegment(sketch, "E38.9.15.0", {"start": v(15.16, 86.65) * mm, "end": v(10.53, 86.65) * mm});
            skLineSegment(sketch, "E38.9.15.1", {"start": v(15.16, 86.65) * mm, "end": v(15.16, 91.27) * mm});
            skLineSegment(sketch, "E38.9.15.2", {"start": v(10.53, 86.65) * mm, "end": v(10.53, 91.27) * mm});
            skLineSegment(sketch, "E38.9.15.3", {"start": v(15.16, 91.27) * mm, "end": v(10.53, 91.27) * mm});
            skLineSegment(sketch, "E38.9.16.0", {"start": v(15.16, 99.35) * mm, "end": v(10.53, 99.35) * mm});
            skLineSegment(sketch, "E38.9.16.1", {"start": v(15.16, 99.35) * mm, "end": v(15.16, 103.97) * mm});
            skLineSegment(sketch, "E38.9.16.2", {"start": v(10.53, 99.35) * mm, "end": v(10.53, 103.97) * mm});
            skLineSegment(sketch, "E38.9.16.3", {"start": v(15.16, 103.97) * mm, "end": v(10.53, 103.97) * mm});
            skLineSegment(sketch, "E38.10.0.0", {"start": v(27.86, -103.85) * mm, "end": v(23.23, -103.85) * mm});
            skLineSegment(sketch, "E38.10.0.1", {"start": v(27.86, -103.85) * mm, "end": v(27.86, -99.23) * mm});
            skLineSegment(sketch, "E38.10.0.2", {"start": v(23.23, -103.85) * mm, "end": v(23.23, -99.23) * mm});
            skLineSegment(sketch, "E38.10.0.3", {"start": v(27.86, -99.23) * mm, "end": v(23.23, -99.23) * mm});
            skLineSegment(sketch, "E38.10.1.0", {"start": v(27.86, -91.15) * mm, "end": v(23.23, -91.15) * mm});
            skLineSegment(sketch, "E38.10.1.1", {"start": v(27.86, -91.15) * mm, "end": v(27.86, -86.53) * mm});
            skLineSegment(sketch, "E38.10.1.2", {"start": v(23.23, -91.15) * mm, "end": v(23.23, -86.53) * mm});
            skLineSegment(sketch, "E38.10.1.3", {"start": v(27.86, -86.53) * mm, "end": v(23.23, -86.53) * mm});
            skLineSegment(sketch, "E38.10.2.0", {"start": v(27.86, -78.45) * mm, "end": v(23.23, -78.45) * mm});
            skLineSegment(sketch, "E38.10.2.1", {"start": v(27.86, -78.45) * mm, "end": v(27.86, -73.83) * mm});
            skLineSegment(sketch, "E38.10.2.2", {"start": v(23.23, -78.45) * mm, "end": v(23.23, -73.83) * mm});
            skLineSegment(sketch, "E38.10.2.3", {"start": v(27.86, -73.83) * mm, "end": v(23.23, -73.83) * mm});
            skLineSegment(sketch, "E38.10.3.0", {"start": v(27.86, -65.75) * mm, "end": v(23.23, -65.75) * mm});
            skLineSegment(sketch, "E38.10.3.1", {"start": v(27.86, -65.75) * mm, "end": v(27.86, -61.13) * mm});
            skLineSegment(sketch, "E38.10.3.2", {"start": v(23.23, -65.75) * mm, "end": v(23.23, -61.13) * mm});
            skLineSegment(sketch, "E38.10.3.3", {"start": v(27.86, -61.13) * mm, "end": v(23.23, -61.13) * mm});
            skLineSegment(sketch, "E38.10.4.0", {"start": v(27.86, -53.05) * mm, "end": v(23.23, -53.05) * mm});
            skLineSegment(sketch, "E38.10.4.1", {"start": v(27.86, -53.05) * mm, "end": v(27.86, -48.43) * mm});
            skLineSegment(sketch, "E38.10.4.2", {"start": v(23.23, -53.05) * mm, "end": v(23.23, -48.43) * mm});
            skLineSegment(sketch, "E38.10.4.3", {"start": v(27.86, -48.43) * mm, "end": v(23.23, -48.43) * mm});
            skLineSegment(sketch, "E38.10.5.0", {"start": v(27.86, -40.35) * mm, "end": v(23.23, -40.35) * mm});
            skLineSegment(sketch, "E38.10.5.1", {"start": v(27.86, -40.35) * mm, "end": v(27.86, -35.73) * mm});
            skLineSegment(sketch, "E38.10.5.2", {"start": v(23.23, -40.35) * mm, "end": v(23.23, -35.73) * mm});
            skLineSegment(sketch, "E38.10.5.3", {"start": v(27.86, -35.73) * mm, "end": v(23.23, -35.73) * mm});
            skLineSegment(sketch, "E38.10.6.0", {"start": v(27.86, -27.65) * mm, "end": v(23.23, -27.65) * mm});
            skLineSegment(sketch, "E38.10.6.1", {"start": v(27.86, -27.65) * mm, "end": v(27.86, -23.03) * mm});
            skLineSegment(sketch, "E38.10.6.2", {"start": v(23.23, -27.65) * mm, "end": v(23.23, -23.03) * mm});
            skLineSegment(sketch, "E38.10.6.3", {"start": v(27.86, -23.03) * mm, "end": v(23.23, -23.03) * mm});
            skLineSegment(sketch, "E38.10.7.0", {"start": v(27.86, -14.95) * mm, "end": v(23.23, -14.95) * mm});
            skLineSegment(sketch, "E38.10.7.1", {"start": v(27.86, -14.95) * mm, "end": v(27.86, -10.33) * mm});
            skLineSegment(sketch, "E38.10.7.2", {"start": v(23.23, -14.95) * mm, "end": v(23.23, -10.33) * mm});
            skLineSegment(sketch, "E38.10.7.3", {"start": v(27.86, -10.33) * mm, "end": v(23.23, -10.33) * mm});
            skLineSegment(sketch, "E38.10.8.0", {"start": v(27.86, -2.25) * mm, "end": v(23.23, -2.25) * mm});
            skLineSegment(sketch, "E38.10.8.1", {"start": v(27.86, -2.25) * mm, "end": v(27.86, 2.37) * mm});
            skLineSegment(sketch, "E38.10.8.2", {"start": v(23.23, -2.25) * mm, "end": v(23.23, 2.37) * mm});
            skLineSegment(sketch, "E38.10.8.3", {"start": v(27.86, 2.37) * mm, "end": v(23.23, 2.37) * mm});
            skLineSegment(sketch, "E38.10.9.0", {"start": v(27.86, 10.45) * mm, "end": v(23.23, 10.45) * mm});
            skLineSegment(sketch, "E38.10.9.1", {"start": v(27.86, 10.45) * mm, "end": v(27.86, 15.07) * mm});
            skLineSegment(sketch, "E38.10.9.2", {"start": v(23.23, 10.45) * mm, "end": v(23.23, 15.07) * mm});
            skLineSegment(sketch, "E38.10.9.3", {"start": v(27.86, 15.07) * mm, "end": v(23.23, 15.07) * mm});
            skLineSegment(sketch, "E38.10.10.0", {"start": v(27.86, 23.15) * mm, "end": v(23.23, 23.15) * mm});
            skLineSegment(sketch, "E38.10.10.1", {"start": v(27.86, 23.15) * mm, "end": v(27.86, 27.77) * mm});
            skLineSegment(sketch, "E38.10.10.2", {"start": v(23.23, 23.15) * mm, "end": v(23.23, 27.77) * mm});
            skLineSegment(sketch, "E38.10.10.3", {"start": v(27.86, 27.77) * mm, "end": v(23.23, 27.77) * mm});
            skLineSegment(sketch, "E38.10.11.0", {"start": v(27.86, 35.85) * mm, "end": v(23.23, 35.85) * mm});
            skLineSegment(sketch, "E38.10.11.1", {"start": v(27.86, 35.85) * mm, "end": v(27.86, 40.47) * mm});
            skLineSegment(sketch, "E38.10.11.2", {"start": v(23.23, 35.85) * mm, "end": v(23.23, 40.47) * mm});
            skLineSegment(sketch, "E38.10.11.3", {"start": v(27.86, 40.47) * mm, "end": v(23.23, 40.47) * mm});
            skLineSegment(sketch, "E38.10.12.0", {"start": v(27.86, 48.55) * mm, "end": v(23.23, 48.55) * mm});
            skLineSegment(sketch, "E38.10.12.1", {"start": v(27.86, 48.55) * mm, "end": v(27.86, 53.17) * mm});
            skLineSegment(sketch, "E38.10.12.2", {"start": v(23.23, 48.55) * mm, "end": v(23.23, 53.17) * mm});
            skLineSegment(sketch, "E38.10.12.3", {"start": v(27.86, 53.17) * mm, "end": v(23.23, 53.17) * mm});
            skLineSegment(sketch, "E38.10.13.0", {"start": v(27.86, 61.25) * mm, "end": v(23.23, 61.25) * mm});
            skLineSegment(sketch, "E38.10.13.1", {"start": v(27.86, 61.25) * mm, "end": v(27.86, 65.87) * mm});
            skLineSegment(sketch, "E38.10.13.2", {"start": v(23.23, 61.25) * mm, "end": v(23.23, 65.87) * mm});
            skLineSegment(sketch, "E38.10.13.3", {"start": v(27.86, 65.87) * mm, "end": v(23.23, 65.87) * mm});
            skLineSegment(sketch, "E38.10.14.0", {"start": v(27.86, 73.95) * mm, "end": v(23.23, 73.95) * mm});
            skLineSegment(sketch, "E38.10.14.1", {"start": v(27.86, 73.95) * mm, "end": v(27.86, 78.57) * mm});
            skLineSegment(sketch, "E38.10.14.2", {"start": v(23.23, 73.95) * mm, "end": v(23.23, 78.57) * mm});
            skLineSegment(sketch, "E38.10.14.3", {"start": v(27.86, 78.57) * mm, "end": v(23.23, 78.57) * mm});
            skLineSegment(sketch, "E38.10.15.0", {"start": v(27.86, 86.65) * mm, "end": v(23.23, 86.65) * mm});
            skLineSegment(sketch, "E38.10.15.1", {"start": v(27.86, 86.65) * mm, "end": v(27.86, 91.27) * mm});
            skLineSegment(sketch, "E38.10.15.2", {"start": v(23.23, 86.65) * mm, "end": v(23.23, 91.27) * mm});
            skLineSegment(sketch, "E38.10.15.3", {"start": v(27.86, 91.27) * mm, "end": v(23.23, 91.27) * mm});
            skLineSegment(sketch, "E38.10.16.0", {"start": v(27.86, 99.35) * mm, "end": v(23.23, 99.35) * mm});
            skLineSegment(sketch, "E38.10.16.1", {"start": v(27.86, 99.35) * mm, "end": v(27.86, 103.97) * mm});
            skLineSegment(sketch, "E38.10.16.2", {"start": v(23.23, 99.35) * mm, "end": v(23.23, 103.97) * mm});
            skLineSegment(sketch, "E38.10.16.3", {"start": v(27.86, 103.97) * mm, "end": v(23.23, 103.97) * mm});
            skLineSegment(sketch, "E38.11.0.0", {"start": v(40.56, -103.85) * mm, "end": v(35.93, -103.85) * mm});
            skLineSegment(sketch, "E38.11.0.1", {"start": v(40.56, -103.85) * mm, "end": v(40.56, -99.23) * mm});
            skLineSegment(sketch, "E38.11.0.2", {"start": v(35.93, -103.85) * mm, "end": v(35.93, -99.23) * mm});
            skLineSegment(sketch, "E38.11.0.3", {"start": v(40.56, -99.23) * mm, "end": v(35.93, -99.23) * mm});
            skLineSegment(sketch, "E38.11.1.0", {"start": v(40.56, -91.15) * mm, "end": v(35.93, -91.15) * mm});
            skLineSegment(sketch, "E38.11.1.1", {"start": v(40.56, -91.15) * mm, "end": v(40.56, -86.53) * mm});
            skLineSegment(sketch, "E38.11.1.2", {"start": v(35.93, -91.15) * mm, "end": v(35.93, -86.53) * mm});
            skLineSegment(sketch, "E38.11.1.3", {"start": v(40.56, -86.53) * mm, "end": v(35.93, -86.53) * mm});
            skLineSegment(sketch, "E38.11.2.0", {"start": v(40.56, -78.45) * mm, "end": v(35.93, -78.45) * mm});
            skLineSegment(sketch, "E38.11.2.1", {"start": v(40.56, -78.45) * mm, "end": v(40.56, -73.83) * mm});
            skLineSegment(sketch, "E38.11.2.2", {"start": v(35.93, -78.45) * mm, "end": v(35.93, -73.83) * mm});
            skLineSegment(sketch, "E38.11.2.3", {"start": v(40.56, -73.83) * mm, "end": v(35.93, -73.83) * mm});
            skLineSegment(sketch, "E38.11.3.0", {"start": v(40.56, -65.75) * mm, "end": v(35.93, -65.75) * mm});
            skLineSegment(sketch, "E38.11.3.1", {"start": v(40.56, -65.75) * mm, "end": v(40.56, -61.13) * mm});
            skLineSegment(sketch, "E38.11.3.2", {"start": v(35.93, -65.75) * mm, "end": v(35.93, -61.13) * mm});
            skLineSegment(sketch, "E38.11.3.3", {"start": v(40.56, -61.13) * mm, "end": v(35.93, -61.13) * mm});
            skLineSegment(sketch, "E38.11.4.0", {"start": v(40.56, -53.05) * mm, "end": v(35.93, -53.05) * mm});
            skLineSegment(sketch, "E38.11.4.1", {"start": v(40.56, -53.05) * mm, "end": v(40.56, -48.43) * mm});
            skLineSegment(sketch, "E38.11.4.2", {"start": v(35.93, -53.05) * mm, "end": v(35.93, -48.43) * mm});
            skLineSegment(sketch, "E38.11.4.3", {"start": v(40.56, -48.43) * mm, "end": v(35.93, -48.43) * mm});
            skLineSegment(sketch, "E38.11.5.0", {"start": v(40.56, -40.35) * mm, "end": v(35.93, -40.35) * mm});
            skLineSegment(sketch, "E38.11.5.1", {"start": v(40.56, -40.35) * mm, "end": v(40.56, -35.73) * mm});
            skLineSegment(sketch, "E38.11.5.2", {"start": v(35.93, -40.35) * mm, "end": v(35.93, -35.73) * mm});
            skLineSegment(sketch, "E38.11.5.3", {"start": v(40.56, -35.73) * mm, "end": v(35.93, -35.73) * mm});
            skLineSegment(sketch, "E38.11.6.0", {"start": v(40.56, -27.65) * mm, "end": v(35.93, -27.65) * mm});
            skLineSegment(sketch, "E38.11.6.1", {"start": v(40.56, -27.65) * mm, "end": v(40.56, -23.03) * mm});
            skLineSegment(sketch, "E38.11.6.2", {"start": v(35.93, -27.65) * mm, "end": v(35.93, -23.03) * mm});
            skLineSegment(sketch, "E38.11.6.3", {"start": v(40.56, -23.03) * mm, "end": v(35.93, -23.03) * mm});
            skLineSegment(sketch, "E38.11.7.0", {"start": v(40.56, -14.95) * mm, "end": v(35.93, -14.95) * mm});
            skLineSegment(sketch, "E38.11.7.1", {"start": v(40.56, -14.95) * mm, "end": v(40.56, -10.33) * mm});
            skLineSegment(sketch, "E38.11.7.2", {"start": v(35.93, -14.95) * mm, "end": v(35.93, -10.33) * mm});
            skLineSegment(sketch, "E38.11.7.3", {"start": v(40.56, -10.33) * mm, "end": v(35.93, -10.33) * mm});
            skLineSegment(sketch, "E38.11.8.0", {"start": v(40.56, -2.25) * mm, "end": v(35.93, -2.25) * mm});
            skLineSegment(sketch, "E38.11.8.1", {"start": v(40.56, -2.25) * mm, "end": v(40.56, 2.37) * mm});
            skLineSegment(sketch, "E38.11.8.2", {"start": v(35.93, -2.25) * mm, "end": v(35.93, 2.37) * mm});
            skLineSegment(sketch, "E38.11.8.3", {"start": v(40.56, 2.37) * mm, "end": v(35.93, 2.37) * mm});
            skLineSegment(sketch, "E38.11.9.0", {"start": v(40.56, 10.45) * mm, "end": v(35.93, 10.45) * mm});
            skLineSegment(sketch, "E38.11.9.1", {"start": v(40.56, 10.45) * mm, "end": v(40.56, 15.07) * mm});
            skLineSegment(sketch, "E38.11.9.2", {"start": v(35.93, 10.45) * mm, "end": v(35.93, 15.07) * mm});
            skLineSegment(sketch, "E38.11.9.3", {"start": v(40.56, 15.07) * mm, "end": v(35.93, 15.07) * mm});
            skLineSegment(sketch, "E38.11.10.0", {"start": v(40.56, 23.15) * mm, "end": v(35.93, 23.15) * mm});
            skLineSegment(sketch, "E38.11.10.1", {"start": v(40.56, 23.15) * mm, "end": v(40.56, 27.77) * mm});
            skLineSegment(sketch, "E38.11.10.2", {"start": v(35.93, 23.15) * mm, "end": v(35.93, 27.77) * mm});
            skLineSegment(sketch, "E38.11.10.3", {"start": v(40.56, 27.77) * mm, "end": v(35.93, 27.77) * mm});
            skLineSegment(sketch, "E38.11.11.0", {"start": v(40.56, 35.85) * mm, "end": v(35.93, 35.85) * mm});
            skLineSegment(sketch, "E38.11.11.1", {"start": v(40.56, 35.85) * mm, "end": v(40.56, 40.47) * mm});
            skLineSegment(sketch, "E38.11.11.2", {"start": v(35.93, 35.85) * mm, "end": v(35.93, 40.47) * mm});
            skLineSegment(sketch, "E38.11.11.3", {"start": v(40.56, 40.47) * mm, "end": v(35.93, 40.47) * mm});
            skLineSegment(sketch, "E38.11.12.0", {"start": v(40.56, 48.55) * mm, "end": v(35.93, 48.55) * mm});
            skLineSegment(sketch, "E38.11.12.1", {"start": v(40.56, 48.55) * mm, "end": v(40.56, 53.17) * mm});
            skLineSegment(sketch, "E38.11.12.2", {"start": v(35.93, 48.55) * mm, "end": v(35.93, 53.17) * mm});
            skLineSegment(sketch, "E38.11.12.3", {"start": v(40.56, 53.17) * mm, "end": v(35.93, 53.17) * mm});
            skLineSegment(sketch, "E38.11.13.0", {"start": v(40.56, 61.25) * mm, "end": v(35.93, 61.25) * mm});
            skLineSegment(sketch, "E38.11.13.1", {"start": v(40.56, 61.25) * mm, "end": v(40.56, 65.87) * mm});
            skLineSegment(sketch, "E38.11.13.2", {"start": v(35.93, 61.25) * mm, "end": v(35.93, 65.87) * mm});
            skLineSegment(sketch, "E38.11.13.3", {"start": v(40.56, 65.87) * mm, "end": v(35.93, 65.87) * mm});
            skLineSegment(sketch, "E38.11.14.0", {"start": v(40.56, 73.95) * mm, "end": v(35.93, 73.95) * mm});
            skLineSegment(sketch, "E38.11.14.1", {"start": v(40.56, 73.95) * mm, "end": v(40.56, 78.57) * mm});
            skLineSegment(sketch, "E38.11.14.2", {"start": v(35.93, 73.95) * mm, "end": v(35.93, 78.57) * mm});
            skLineSegment(sketch, "E38.11.14.3", {"start": v(40.56, 78.57) * mm, "end": v(35.93, 78.57) * mm});
            skLineSegment(sketch, "E38.11.15.0", {"start": v(40.56, 86.65) * mm, "end": v(35.93, 86.65) * mm});
            skLineSegment(sketch, "E38.11.15.1", {"start": v(40.56, 86.65) * mm, "end": v(40.56, 91.27) * mm});
            skLineSegment(sketch, "E38.11.15.2", {"start": v(35.93, 86.65) * mm, "end": v(35.93, 91.27) * mm});
            skLineSegment(sketch, "E38.11.15.3", {"start": v(40.56, 91.27) * mm, "end": v(35.93, 91.27) * mm});
            skLineSegment(sketch, "E38.11.16.0", {"start": v(40.56, 99.35) * mm, "end": v(35.93, 99.35) * mm});
            skLineSegment(sketch, "E38.11.16.1", {"start": v(40.56, 99.35) * mm, "end": v(40.56, 103.97) * mm});
            skLineSegment(sketch, "E38.11.16.2", {"start": v(35.93, 99.35) * mm, "end": v(35.93, 103.97) * mm});
            skLineSegment(sketch, "E38.11.16.3", {"start": v(40.56, 103.97) * mm, "end": v(35.93, 103.97) * mm});
            skLineSegment(sketch, "E38.12.0.0", {"start": v(53.26, -103.85) * mm, "end": v(48.63, -103.85) * mm});
            skLineSegment(sketch, "E38.12.0.1", {"start": v(53.26, -103.85) * mm, "end": v(53.26, -99.23) * mm});
            skLineSegment(sketch, "E38.12.0.2", {"start": v(48.63, -103.85) * mm, "end": v(48.63, -99.23) * mm});
            skLineSegment(sketch, "E38.12.0.3", {"start": v(53.26, -99.23) * mm, "end": v(48.63, -99.23) * mm});
            skLineSegment(sketch, "E38.12.1.0", {"start": v(53.26, -91.15) * mm, "end": v(48.63, -91.15) * mm});
            skLineSegment(sketch, "E38.12.1.1", {"start": v(53.26, -91.15) * mm, "end": v(53.26, -86.53) * mm});
            skLineSegment(sketch, "E38.12.1.2", {"start": v(48.63, -91.15) * mm, "end": v(48.63, -86.53) * mm});
            skLineSegment(sketch, "E38.12.1.3", {"start": v(53.26, -86.53) * mm, "end": v(48.63, -86.53) * mm});
            skLineSegment(sketch, "E38.12.2.0", {"start": v(53.26, -78.45) * mm, "end": v(48.63, -78.45) * mm});
            skLineSegment(sketch, "E38.12.2.1", {"start": v(53.26, -78.45) * mm, "end": v(53.26, -73.83) * mm});
            skLineSegment(sketch, "E38.12.2.2", {"start": v(48.63, -78.45) * mm, "end": v(48.63, -73.83) * mm});
            skLineSegment(sketch, "E38.12.2.3", {"start": v(53.26, -73.83) * mm, "end": v(48.63, -73.83) * mm});
            skLineSegment(sketch, "E38.12.3.0", {"start": v(53.26, -65.75) * mm, "end": v(48.63, -65.75) * mm});
            skLineSegment(sketch, "E38.12.3.1", {"start": v(53.26, -65.75) * mm, "end": v(53.26, -61.13) * mm});
            skLineSegment(sketch, "E38.12.3.2", {"start": v(48.63, -65.75) * mm, "end": v(48.63, -61.13) * mm});
            skLineSegment(sketch, "E38.12.3.3", {"start": v(53.26, -61.13) * mm, "end": v(48.63, -61.13) * mm});
            skLineSegment(sketch, "E38.12.4.0", {"start": v(53.26, -53.05) * mm, "end": v(48.63, -53.05) * mm});
            skLineSegment(sketch, "E38.12.4.1", {"start": v(53.26, -53.05) * mm, "end": v(53.26, -48.43) * mm});
            skLineSegment(sketch, "E38.12.4.2", {"start": v(48.63, -53.05) * mm, "end": v(48.63, -48.43) * mm});
            skLineSegment(sketch, "E38.12.4.3", {"start": v(53.26, -48.43) * mm, "end": v(48.63, -48.43) * mm});
            skLineSegment(sketch, "E38.12.5.0", {"start": v(53.26, -40.35) * mm, "end": v(48.63, -40.35) * mm});
            skLineSegment(sketch, "E38.12.5.1", {"start": v(53.26, -40.35) * mm, "end": v(53.26, -35.73) * mm});
            skLineSegment(sketch, "E38.12.5.2", {"start": v(48.63, -40.35) * mm, "end": v(48.63, -35.73) * mm});
            skLineSegment(sketch, "E38.12.5.3", {"start": v(53.26, -35.73) * mm, "end": v(48.63, -35.73) * mm});
            skLineSegment(sketch, "E38.12.6.0", {"start": v(53.26, -27.65) * mm, "end": v(48.63, -27.65) * mm});
            skLineSegment(sketch, "E38.12.6.1", {"start": v(53.26, -27.65) * mm, "end": v(53.26, -23.03) * mm});
            skLineSegment(sketch, "E38.12.6.2", {"start": v(48.63, -27.65) * mm, "end": v(48.63, -23.03) * mm});
            skLineSegment(sketch, "E38.12.6.3", {"start": v(53.26, -23.03) * mm, "end": v(48.63, -23.03) * mm});
            skLineSegment(sketch, "E38.12.7.0", {"start": v(53.26, -14.95) * mm, "end": v(48.63, -14.95) * mm});
            skLineSegment(sketch, "E38.12.7.1", {"start": v(53.26, -14.95) * mm, "end": v(53.26, -10.33) * mm});
            skLineSegment(sketch, "E38.12.7.2", {"start": v(48.63, -14.95) * mm, "end": v(48.63, -10.33) * mm});
            skLineSegment(sketch, "E38.12.7.3", {"start": v(53.26, -10.33) * mm, "end": v(48.63, -10.33) * mm});
            skLineSegment(sketch, "E38.12.8.0", {"start": v(53.26, -2.25) * mm, "end": v(48.63, -2.25) * mm});
            skLineSegment(sketch, "E38.12.8.1", {"start": v(53.26, -2.25) * mm, "end": v(53.26, 2.37) * mm});
            skLineSegment(sketch, "E38.12.8.2", {"start": v(48.63, -2.25) * mm, "end": v(48.63, 2.37) * mm});
            skLineSegment(sketch, "E38.12.8.3", {"start": v(53.26, 2.37) * mm, "end": v(48.63, 2.37) * mm});
            skLineSegment(sketch, "E38.12.9.0", {"start": v(53.26, 10.45) * mm, "end": v(48.63, 10.45) * mm});
            skLineSegment(sketch, "E38.12.9.1", {"start": v(53.26, 10.45) * mm, "end": v(53.26, 15.07) * mm});
            skLineSegment(sketch, "E38.12.9.2", {"start": v(48.63, 10.45) * mm, "end": v(48.63, 15.07) * mm});
            skLineSegment(sketch, "E38.12.9.3", {"start": v(53.26, 15.07) * mm, "end": v(48.63, 15.07) * mm});
            skLineSegment(sketch, "E38.12.10.0", {"start": v(53.26, 23.15) * mm, "end": v(48.63, 23.15) * mm});
            skLineSegment(sketch, "E38.12.10.1", {"start": v(53.26, 23.15) * mm, "end": v(53.26, 27.77) * mm});
            skLineSegment(sketch, "E38.12.10.2", {"start": v(48.63, 23.15) * mm, "end": v(48.63, 27.77) * mm});
            skLineSegment(sketch, "E38.12.10.3", {"start": v(53.26, 27.77) * mm, "end": v(48.63, 27.77) * mm});
            skLineSegment(sketch, "E38.12.11.0", {"start": v(53.26, 35.85) * mm, "end": v(48.63, 35.85) * mm});
            skLineSegment(sketch, "E38.12.11.1", {"start": v(53.26, 35.85) * mm, "end": v(53.26, 40.47) * mm});
            skLineSegment(sketch, "E38.12.11.2", {"start": v(48.63, 35.85) * mm, "end": v(48.63, 40.47) * mm});
            skLineSegment(sketch, "E38.12.11.3", {"start": v(53.26, 40.47) * mm, "end": v(48.63, 40.47) * mm});
            skLineSegment(sketch, "E38.12.12.0", {"start": v(53.26, 48.55) * mm, "end": v(48.63, 48.55) * mm});
            skLineSegment(sketch, "E38.12.12.1", {"start": v(53.26, 48.55) * mm, "end": v(53.26, 53.17) * mm});
            skLineSegment(sketch, "E38.12.12.2", {"start": v(48.63, 48.55) * mm, "end": v(48.63, 53.17) * mm});
            skLineSegment(sketch, "E38.12.12.3", {"start": v(53.26, 53.17) * mm, "end": v(48.63, 53.17) * mm});
            skLineSegment(sketch, "E38.12.13.0", {"start": v(53.26, 61.25) * mm, "end": v(48.63, 61.25) * mm});
            skLineSegment(sketch, "E38.12.13.1", {"start": v(53.26, 61.25) * mm, "end": v(53.26, 65.87) * mm});
            skLineSegment(sketch, "E38.12.13.2", {"start": v(48.63, 61.25) * mm, "end": v(48.63, 65.87) * mm});
            skLineSegment(sketch, "E38.12.13.3", {"start": v(53.26, 65.87) * mm, "end": v(48.63, 65.87) * mm});
            skLineSegment(sketch, "E38.12.14.0", {"start": v(53.26, 73.95) * mm, "end": v(48.63, 73.95) * mm});
            skLineSegment(sketch, "E38.12.14.1", {"start": v(53.26, 73.95) * mm, "end": v(53.26, 78.57) * mm});
            skLineSegment(sketch, "E38.12.14.2", {"start": v(48.63, 73.95) * mm, "end": v(48.63, 78.57) * mm});
            skLineSegment(sketch, "E38.12.14.3", {"start": v(53.26, 78.57) * mm, "end": v(48.63, 78.57) * mm});
            skLineSegment(sketch, "E38.12.15.0", {"start": v(53.26, 86.65) * mm, "end": v(48.63, 86.65) * mm});
            skLineSegment(sketch, "E38.12.15.1", {"start": v(53.26, 86.65) * mm, "end": v(53.26, 91.27) * mm});
            skLineSegment(sketch, "E38.12.15.2", {"start": v(48.63, 86.65) * mm, "end": v(48.63, 91.27) * mm});
            skLineSegment(sketch, "E38.12.15.3", {"start": v(53.26, 91.27) * mm, "end": v(48.63, 91.27) * mm});
            skLineSegment(sketch, "E38.12.16.0", {"start": v(53.26, 99.35) * mm, "end": v(48.63, 99.35) * mm});
            skLineSegment(sketch, "E38.12.16.1", {"start": v(53.26, 99.35) * mm, "end": v(53.26, 103.97) * mm});
            skLineSegment(sketch, "E38.12.16.2", {"start": v(48.63, 99.35) * mm, "end": v(48.63, 103.97) * mm});
            skLineSegment(sketch, "E38.12.16.3", {"start": v(53.26, 103.97) * mm, "end": v(48.63, 103.97) * mm});
            skLineSegment(sketch, "E38.13.0.0", {"start": v(65.96, -103.85) * mm, "end": v(61.33, -103.85) * mm});
            skLineSegment(sketch, "E38.13.0.1", {"start": v(65.96, -103.85) * mm, "end": v(65.96, -99.23) * mm});
            skLineSegment(sketch, "E38.13.0.2", {"start": v(61.33, -103.85) * mm, "end": v(61.33, -99.23) * mm});
            skLineSegment(sketch, "E38.13.0.3", {"start": v(65.96, -99.23) * mm, "end": v(61.33, -99.23) * mm});
            skLineSegment(sketch, "E38.13.1.0", {"start": v(65.96, -91.15) * mm, "end": v(61.33, -91.15) * mm});
            skLineSegment(sketch, "E38.13.1.1", {"start": v(65.96, -91.15) * mm, "end": v(65.96, -86.53) * mm});
            skLineSegment(sketch, "E38.13.1.2", {"start": v(61.33, -91.15) * mm, "end": v(61.33, -86.53) * mm});
            skLineSegment(sketch, "E38.13.1.3", {"start": v(65.96, -86.53) * mm, "end": v(61.33, -86.53) * mm});
            skLineSegment(sketch, "E38.13.2.0", {"start": v(65.96, -78.45) * mm, "end": v(61.33, -78.45) * mm});
            skLineSegment(sketch, "E38.13.2.1", {"start": v(65.96, -78.45) * mm, "end": v(65.96, -73.83) * mm});
            skLineSegment(sketch, "E38.13.2.2", {"start": v(61.33, -78.45) * mm, "end": v(61.33, -73.83) * mm});
            skLineSegment(sketch, "E38.13.2.3", {"start": v(65.96, -73.83) * mm, "end": v(61.33, -73.83) * mm});
            skLineSegment(sketch, "E38.13.3.0", {"start": v(65.96, -65.75) * mm, "end": v(61.33, -65.75) * mm});
            skLineSegment(sketch, "E38.13.3.1", {"start": v(65.96, -65.75) * mm, "end": v(65.96, -61.13) * mm});
            skLineSegment(sketch, "E38.13.3.2", {"start": v(61.33, -65.75) * mm, "end": v(61.33, -61.13) * mm});
            skLineSegment(sketch, "E38.13.3.3", {"start": v(65.96, -61.13) * mm, "end": v(61.33, -61.13) * mm});
            skLineSegment(sketch, "E38.13.4.0", {"start": v(65.96, -53.05) * mm, "end": v(61.33, -53.05) * mm});
            skLineSegment(sketch, "E38.13.4.1", {"start": v(65.96, -53.05) * mm, "end": v(65.96, -48.43) * mm});
            skLineSegment(sketch, "E38.13.4.2", {"start": v(61.33, -53.05) * mm, "end": v(61.33, -48.43) * mm});
            skLineSegment(sketch, "E38.13.4.3", {"start": v(65.96, -48.43) * mm, "end": v(61.33, -48.43) * mm});
            skLineSegment(sketch, "E38.13.5.0", {"start": v(65.96, -40.35) * mm, "end": v(61.33, -40.35) * mm});
            skLineSegment(sketch, "E38.13.5.1", {"start": v(65.96, -40.35) * mm, "end": v(65.96, -35.73) * mm});
            skLineSegment(sketch, "E38.13.5.2", {"start": v(61.33, -40.35) * mm, "end": v(61.33, -35.73) * mm});
            skLineSegment(sketch, "E38.13.5.3", {"start": v(65.96, -35.73) * mm, "end": v(61.33, -35.73) * mm});
            skLineSegment(sketch, "E38.13.6.0", {"start": v(65.96, -27.65) * mm, "end": v(61.33, -27.65) * mm});
            skLineSegment(sketch, "E38.13.6.1", {"start": v(65.96, -27.65) * mm, "end": v(65.96, -23.03) * mm});
            skLineSegment(sketch, "E38.13.6.2", {"start": v(61.33, -27.65) * mm, "end": v(61.33, -23.03) * mm});
            skLineSegment(sketch, "E38.13.6.3", {"start": v(65.96, -23.03) * mm, "end": v(61.33, -23.03) * mm});
            skLineSegment(sketch, "E38.13.7.0", {"start": v(65.96, -14.95) * mm, "end": v(61.33, -14.95) * mm});
            skLineSegment(sketch, "E38.13.7.1", {"start": v(65.96, -14.95) * mm, "end": v(65.96, -10.33) * mm});
            skLineSegment(sketch, "E38.13.7.2", {"start": v(61.33, -14.95) * mm, "end": v(61.33, -10.33) * mm});
            skLineSegment(sketch, "E38.13.7.3", {"start": v(65.96, -10.33) * mm, "end": v(61.33, -10.33) * mm});
            skLineSegment(sketch, "E38.13.8.0", {"start": v(65.96, -2.25) * mm, "end": v(61.33, -2.25) * mm});
            skLineSegment(sketch, "E38.13.8.1", {"start": v(65.96, -2.25) * mm, "end": v(65.96, 2.37) * mm});
            skLineSegment(sketch, "E38.13.8.2", {"start": v(61.33, -2.25) * mm, "end": v(61.33, 2.37) * mm});
            skLineSegment(sketch, "E38.13.8.3", {"start": v(65.96, 2.37) * mm, "end": v(61.33, 2.37) * mm});
            skLineSegment(sketch, "E38.13.9.0", {"start": v(65.96, 10.45) * mm, "end": v(61.33, 10.45) * mm});
            skLineSegment(sketch, "E38.13.9.1", {"start": v(65.96, 10.45) * mm, "end": v(65.96, 15.07) * mm});
            skLineSegment(sketch, "E38.13.9.2", {"start": v(61.33, 10.45) * mm, "end": v(61.33, 15.07) * mm});
            skLineSegment(sketch, "E38.13.9.3", {"start": v(65.96, 15.07) * mm, "end": v(61.33, 15.07) * mm});
            skLineSegment(sketch, "E38.13.10.0", {"start": v(65.96, 23.15) * mm, "end": v(61.33, 23.15) * mm});
            skLineSegment(sketch, "E38.13.10.1", {"start": v(65.96, 23.15) * mm, "end": v(65.96, 27.77) * mm});
            skLineSegment(sketch, "E38.13.10.2", {"start": v(61.33, 23.15) * mm, "end": v(61.33, 27.77) * mm});
            skLineSegment(sketch, "E38.13.10.3", {"start": v(65.96, 27.77) * mm, "end": v(61.33, 27.77) * mm});
            skLineSegment(sketch, "E38.13.11.0", {"start": v(65.96, 35.85) * mm, "end": v(61.33, 35.85) * mm});
            skLineSegment(sketch, "E38.13.11.1", {"start": v(65.96, 35.85) * mm, "end": v(65.96, 40.47) * mm});
            skLineSegment(sketch, "E38.13.11.2", {"start": v(61.33, 35.85) * mm, "end": v(61.33, 40.47) * mm});
            skLineSegment(sketch, "E38.13.11.3", {"start": v(65.96, 40.47) * mm, "end": v(61.33, 40.47) * mm});
            skLineSegment(sketch, "E38.13.12.0", {"start": v(65.96, 48.55) * mm, "end": v(61.33, 48.55) * mm});
            skLineSegment(sketch, "E38.13.12.1", {"start": v(65.96, 48.55) * mm, "end": v(65.96, 53.17) * mm});
            skLineSegment(sketch, "E38.13.12.2", {"start": v(61.33, 48.55) * mm, "end": v(61.33, 53.17) * mm});
            skLineSegment(sketch, "E38.13.12.3", {"start": v(65.96, 53.17) * mm, "end": v(61.33, 53.17) * mm});
            skLineSegment(sketch, "E38.13.13.0", {"start": v(65.96, 61.25) * mm, "end": v(61.33, 61.25) * mm});
            skLineSegment(sketch, "E38.13.13.1", {"start": v(65.96, 61.25) * mm, "end": v(65.96, 65.87) * mm});
            skLineSegment(sketch, "E38.13.13.2", {"start": v(61.33, 61.25) * mm, "end": v(61.33, 65.87) * mm});
            skLineSegment(sketch, "E38.13.13.3", {"start": v(65.96, 65.87) * mm, "end": v(61.33, 65.87) * mm});
            skLineSegment(sketch, "E38.13.14.0", {"start": v(65.96, 73.95) * mm, "end": v(61.33, 73.95) * mm});
            skLineSegment(sketch, "E38.13.14.1", {"start": v(65.96, 73.95) * mm, "end": v(65.96, 78.57) * mm});
            skLineSegment(sketch, "E38.13.14.2", {"start": v(61.33, 73.95) * mm, "end": v(61.33, 78.57) * mm});
            skLineSegment(sketch, "E38.13.14.3", {"start": v(65.96, 78.57) * mm, "end": v(61.33, 78.57) * mm});
            skLineSegment(sketch, "E38.13.15.0", {"start": v(65.96, 86.65) * mm, "end": v(61.33, 86.65) * mm});
            skLineSegment(sketch, "E38.13.15.1", {"start": v(65.96, 86.65) * mm, "end": v(65.96, 91.27) * mm});
            skLineSegment(sketch, "E38.13.15.2", {"start": v(61.33, 86.65) * mm, "end": v(61.33, 91.27) * mm});
            skLineSegment(sketch, "E38.13.15.3", {"start": v(65.96, 91.27) * mm, "end": v(61.33, 91.27) * mm});
            skLineSegment(sketch, "E38.13.16.0", {"start": v(65.96, 99.35) * mm, "end": v(61.33, 99.35) * mm});
            skLineSegment(sketch, "E38.13.16.1", {"start": v(65.96, 99.35) * mm, "end": v(65.96, 103.97) * mm});
            skLineSegment(sketch, "E38.13.16.2", {"start": v(61.33, 99.35) * mm, "end": v(61.33, 103.97) * mm});
            skLineSegment(sketch, "E38.13.16.3", {"start": v(65.96, 103.97) * mm, "end": v(61.33, 103.97) * mm});
            skLineSegment(sketch, "E38.14.0.0", {"start": v(78.66, -103.85) * mm, "end": v(74.03, -103.85) * mm});
            skLineSegment(sketch, "E38.14.0.1", {"start": v(78.66, -103.85) * mm, "end": v(78.66, -99.23) * mm});
            skLineSegment(sketch, "E38.14.0.2", {"start": v(74.03, -103.85) * mm, "end": v(74.03, -99.23) * mm});
            skLineSegment(sketch, "E38.14.0.3", {"start": v(78.66, -99.23) * mm, "end": v(74.03, -99.23) * mm});
            skLineSegment(sketch, "E38.14.1.0", {"start": v(78.66, -91.15) * mm, "end": v(74.03, -91.15) * mm});
            skLineSegment(sketch, "E38.14.1.1", {"start": v(78.66, -91.15) * mm, "end": v(78.66, -86.53) * mm});
            skLineSegment(sketch, "E38.14.1.2", {"start": v(74.03, -91.15) * mm, "end": v(74.03, -86.53) * mm});
            skLineSegment(sketch, "E38.14.1.3", {"start": v(78.66, -86.53) * mm, "end": v(74.03, -86.53) * mm});
            skLineSegment(sketch, "E38.14.2.0", {"start": v(78.66, -78.45) * mm, "end": v(74.03, -78.45) * mm});
            skLineSegment(sketch, "E38.14.2.1", {"start": v(78.66, -78.45) * mm, "end": v(78.66, -73.83) * mm});
            skLineSegment(sketch, "E38.14.2.2", {"start": v(74.03, -78.45) * mm, "end": v(74.03, -73.83) * mm});
            skLineSegment(sketch, "E38.14.2.3", {"start": v(78.66, -73.83) * mm, "end": v(74.03, -73.83) * mm});
            skLineSegment(sketch, "E38.14.3.0", {"start": v(78.66, -65.75) * mm, "end": v(74.03, -65.75) * mm});
            skLineSegment(sketch, "E38.14.3.1", {"start": v(78.66, -65.75) * mm, "end": v(78.66, -61.13) * mm});
            skLineSegment(sketch, "E38.14.3.2", {"start": v(74.03, -65.75) * mm, "end": v(74.03, -61.13) * mm});
            skLineSegment(sketch, "E38.14.3.3", {"start": v(78.66, -61.13) * mm, "end": v(74.03, -61.13) * mm});
            skLineSegment(sketch, "E38.14.4.0", {"start": v(78.66, -53.05) * mm, "end": v(74.03, -53.05) * mm});
            skLineSegment(sketch, "E38.14.4.1", {"start": v(78.66, -53.05) * mm, "end": v(78.66, -48.43) * mm});
            skLineSegment(sketch, "E38.14.4.2", {"start": v(74.03, -53.05) * mm, "end": v(74.03, -48.43) * mm});
            skLineSegment(sketch, "E38.14.4.3", {"start": v(78.66, -48.43) * mm, "end": v(74.03, -48.43) * mm});
            skLineSegment(sketch, "E38.14.5.0", {"start": v(78.66, -40.35) * mm, "end": v(74.03, -40.35) * mm});
            skLineSegment(sketch, "E38.14.5.1", {"start": v(78.66, -40.35) * mm, "end": v(78.66, -35.73) * mm});
            skLineSegment(sketch, "E38.14.5.2", {"start": v(74.03, -40.35) * mm, "end": v(74.03, -35.73) * mm});
            skLineSegment(sketch, "E38.14.5.3", {"start": v(78.66, -35.73) * mm, "end": v(74.03, -35.73) * mm});
            skLineSegment(sketch, "E38.14.6.0", {"start": v(78.66, -27.65) * mm, "end": v(74.03, -27.65) * mm});
            skLineSegment(sketch, "E38.14.6.1", {"start": v(78.66, -27.65) * mm, "end": v(78.66, -23.03) * mm});
            skLineSegment(sketch, "E38.14.6.2", {"start": v(74.03, -27.65) * mm, "end": v(74.03, -23.03) * mm});
            skLineSegment(sketch, "E38.14.6.3", {"start": v(78.66, -23.03) * mm, "end": v(74.03, -23.03) * mm});
            skLineSegment(sketch, "E38.14.7.0", {"start": v(78.66, -14.95) * mm, "end": v(74.03, -14.95) * mm});
            skLineSegment(sketch, "E38.14.7.1", {"start": v(78.66, -14.95) * mm, "end": v(78.66, -10.33) * mm});
            skLineSegment(sketch, "E38.14.7.2", {"start": v(74.03, -14.95) * mm, "end": v(74.03, -10.33) * mm});
            skLineSegment(sketch, "E38.14.7.3", {"start": v(78.66, -10.33) * mm, "end": v(74.03, -10.33) * mm});
            skLineSegment(sketch, "E38.14.8.0", {"start": v(78.66, -2.25) * mm, "end": v(74.03, -2.25) * mm});
            skLineSegment(sketch, "E38.14.8.1", {"start": v(78.66, -2.25) * mm, "end": v(78.66, 2.37) * mm});
            skLineSegment(sketch, "E38.14.8.2", {"start": v(74.03, -2.25) * mm, "end": v(74.03, 2.37) * mm});
            skLineSegment(sketch, "E38.14.8.3", {"start": v(78.66, 2.37) * mm, "end": v(74.03, 2.37) * mm});
            skLineSegment(sketch, "E38.14.9.0", {"start": v(78.66, 10.45) * mm, "end": v(74.03, 10.45) * mm});
            skLineSegment(sketch, "E38.14.9.1", {"start": v(78.66, 10.45) * mm, "end": v(78.66, 15.07) * mm});
            skLineSegment(sketch, "E38.14.9.2", {"start": v(74.03, 10.45) * mm, "end": v(74.03, 15.07) * mm});
            skLineSegment(sketch, "E38.14.9.3", {"start": v(78.66, 15.07) * mm, "end": v(74.03, 15.07) * mm});
            skLineSegment(sketch, "E38.14.10.0", {"start": v(78.66, 23.15) * mm, "end": v(74.03, 23.15) * mm});
            skLineSegment(sketch, "E38.14.10.1", {"start": v(78.66, 23.15) * mm, "end": v(78.66, 27.77) * mm});
            skLineSegment(sketch, "E38.14.10.2", {"start": v(74.03, 23.15) * mm, "end": v(74.03, 27.77) * mm});
            skLineSegment(sketch, "E38.14.10.3", {"start": v(78.66, 27.77) * mm, "end": v(74.03, 27.77) * mm});
            skLineSegment(sketch, "E38.14.11.0", {"start": v(78.66, 35.85) * mm, "end": v(74.03, 35.85) * mm});
            skLineSegment(sketch, "E38.14.11.1", {"start": v(78.66, 35.85) * mm, "end": v(78.66, 40.47) * mm});
            skLineSegment(sketch, "E38.14.11.2", {"start": v(74.03, 35.85) * mm, "end": v(74.03, 40.47) * mm});
            skLineSegment(sketch, "E38.14.11.3", {"start": v(78.66, 40.47) * mm, "end": v(74.03, 40.47) * mm});
            skLineSegment(sketch, "E38.14.12.0", {"start": v(78.66, 48.55) * mm, "end": v(74.03, 48.55) * mm});
            skLineSegment(sketch, "E38.14.12.1", {"start": v(78.66, 48.55) * mm, "end": v(78.66, 53.17) * mm});
            skLineSegment(sketch, "E38.14.12.2", {"start": v(74.03, 48.55) * mm, "end": v(74.03, 53.17) * mm});
            skLineSegment(sketch, "E38.14.12.3", {"start": v(78.66, 53.17) * mm, "end": v(74.03, 53.17) * mm});
            skLineSegment(sketch, "E38.14.13.0", {"start": v(78.66, 61.25) * mm, "end": v(74.03, 61.25) * mm});
            skLineSegment(sketch, "E38.14.13.1", {"start": v(78.66, 61.25) * mm, "end": v(78.66, 65.87) * mm});
            skLineSegment(sketch, "E38.14.13.2", {"start": v(74.03, 61.25) * mm, "end": v(74.03, 65.87) * mm});
            skLineSegment(sketch, "E38.14.13.3", {"start": v(78.66, 65.87) * mm, "end": v(74.03, 65.87) * mm});
            skLineSegment(sketch, "E38.14.14.0", {"start": v(78.66, 73.95) * mm, "end": v(74.03, 73.95) * mm});
            skLineSegment(sketch, "E38.14.14.1", {"start": v(78.66, 73.95) * mm, "end": v(78.66, 78.57) * mm});
            skLineSegment(sketch, "E38.14.14.2", {"start": v(74.03, 73.95) * mm, "end": v(74.03, 78.57) * mm});
            skLineSegment(sketch, "E38.14.14.3", {"start": v(78.66, 78.57) * mm, "end": v(74.03, 78.57) * mm});
            skLineSegment(sketch, "E38.14.15.0", {"start": v(78.66, 86.65) * mm, "end": v(74.03, 86.65) * mm});
            skLineSegment(sketch, "E38.14.15.1", {"start": v(78.66, 86.65) * mm, "end": v(78.66, 91.27) * mm});
            skLineSegment(sketch, "E38.14.15.2", {"start": v(74.03, 86.65) * mm, "end": v(74.03, 91.27) * mm});
            skLineSegment(sketch, "E38.14.15.3", {"start": v(78.66, 91.27) * mm, "end": v(74.03, 91.27) * mm});
            skLineSegment(sketch, "E38.14.16.0", {"start": v(78.66, 99.35) * mm, "end": v(74.03, 99.35) * mm});
            skLineSegment(sketch, "E38.14.16.1", {"start": v(78.66, 99.35) * mm, "end": v(78.66, 103.97) * mm});
            skLineSegment(sketch, "E38.14.16.2", {"start": v(74.03, 99.35) * mm, "end": v(74.03, 103.97) * mm});
            skLineSegment(sketch, "E38.14.16.3", {"start": v(78.66, 103.97) * mm, "end": v(74.03, 103.97) * mm});
            skLineSegment(sketch, "E38.15.0.0", {"start": v(91.36, -103.85) * mm, "end": v(86.73, -103.85) * mm});
            skLineSegment(sketch, "E38.15.0.1", {"start": v(91.36, -103.85) * mm, "end": v(91.36, -99.23) * mm});
            skLineSegment(sketch, "E38.15.0.2", {"start": v(86.73, -103.85) * mm, "end": v(86.73, -99.23) * mm});
            skLineSegment(sketch, "E38.15.0.3", {"start": v(91.36, -99.23) * mm, "end": v(86.73, -99.23) * mm});
            skLineSegment(sketch, "E38.15.1.0", {"start": v(91.36, -91.15) * mm, "end": v(86.73, -91.15) * mm});
            skLineSegment(sketch, "E38.15.1.1", {"start": v(91.36, -91.15) * mm, "end": v(91.36, -86.53) * mm});
            skLineSegment(sketch, "E38.15.1.2", {"start": v(86.73, -91.15) * mm, "end": v(86.73, -86.53) * mm});
            skLineSegment(sketch, "E38.15.1.3", {"start": v(91.36, -86.53) * mm, "end": v(86.73, -86.53) * mm});
            skLineSegment(sketch, "E38.15.2.0", {"start": v(91.36, -78.45) * mm, "end": v(86.73, -78.45) * mm});
            skLineSegment(sketch, "E38.15.2.1", {"start": v(91.36, -78.45) * mm, "end": v(91.36, -73.83) * mm});
            skLineSegment(sketch, "E38.15.2.2", {"start": v(86.73, -78.45) * mm, "end": v(86.73, -73.83) * mm});
            skLineSegment(sketch, "E38.15.2.3", {"start": v(91.36, -73.83) * mm, "end": v(86.73, -73.83) * mm});
            skLineSegment(sketch, "E38.15.3.0", {"start": v(91.36, -65.75) * mm, "end": v(86.73, -65.75) * mm});
            skLineSegment(sketch, "E38.15.3.1", {"start": v(91.36, -65.75) * mm, "end": v(91.36, -61.13) * mm});
            skLineSegment(sketch, "E38.15.3.2", {"start": v(86.73, -65.75) * mm, "end": v(86.73, -61.13) * mm});
            skLineSegment(sketch, "E38.15.3.3", {"start": v(91.36, -61.13) * mm, "end": v(86.73, -61.13) * mm});
            skLineSegment(sketch, "E38.15.4.0", {"start": v(91.36, -53.05) * mm, "end": v(86.73, -53.05) * mm});
            skLineSegment(sketch, "E38.15.4.1", {"start": v(91.36, -53.05) * mm, "end": v(91.36, -48.43) * mm});
            skLineSegment(sketch, "E38.15.4.2", {"start": v(86.73, -53.05) * mm, "end": v(86.73, -48.43) * mm});
            skLineSegment(sketch, "E38.15.4.3", {"start": v(91.36, -48.43) * mm, "end": v(86.73, -48.43) * mm});
            skLineSegment(sketch, "E38.15.5.0", {"start": v(91.36, -40.35) * mm, "end": v(86.73, -40.35) * mm});
            skLineSegment(sketch, "E38.15.5.1", {"start": v(91.36, -40.35) * mm, "end": v(91.36, -35.73) * mm});
            skLineSegment(sketch, "E38.15.5.2", {"start": v(86.73, -40.35) * mm, "end": v(86.73, -35.73) * mm});
            skLineSegment(sketch, "E38.15.5.3", {"start": v(91.36, -35.73) * mm, "end": v(86.73, -35.73) * mm});
            skLineSegment(sketch, "E38.15.6.0", {"start": v(91.36, -27.65) * mm, "end": v(86.73, -27.65) * mm});
            skLineSegment(sketch, "E38.15.6.1", {"start": v(91.36, -27.65) * mm, "end": v(91.36, -23.03) * mm});
            skLineSegment(sketch, "E38.15.6.2", {"start": v(86.73, -27.65) * mm, "end": v(86.73, -23.03) * mm});
            skLineSegment(sketch, "E38.15.6.3", {"start": v(91.36, -23.03) * mm, "end": v(86.73, -23.03) * mm});
            skLineSegment(sketch, "E38.15.7.0", {"start": v(91.36, -14.95) * mm, "end": v(86.73, -14.95) * mm});
            skLineSegment(sketch, "E38.15.7.1", {"start": v(91.36, -14.95) * mm, "end": v(91.36, -10.33) * mm});
            skLineSegment(sketch, "E38.15.7.2", {"start": v(86.73, -14.95) * mm, "end": v(86.73, -10.33) * mm});
            skLineSegment(sketch, "E38.15.7.3", {"start": v(91.36, -10.33) * mm, "end": v(86.73, -10.33) * mm});
            skLineSegment(sketch, "E38.15.8.0", {"start": v(91.36, -2.25) * mm, "end": v(86.73, -2.25) * mm});
            skLineSegment(sketch, "E38.15.8.1", {"start": v(91.36, -2.25) * mm, "end": v(91.36, 2.37) * mm});
            skLineSegment(sketch, "E38.15.8.2", {"start": v(86.73, -2.25) * mm, "end": v(86.73, 2.37) * mm});
            skLineSegment(sketch, "E38.15.8.3", {"start": v(91.36, 2.37) * mm, "end": v(86.73, 2.37) * mm});
            skLineSegment(sketch, "E38.15.9.0", {"start": v(91.36, 10.45) * mm, "end": v(86.73, 10.45) * mm});
            skLineSegment(sketch, "E38.15.9.1", {"start": v(91.36, 10.45) * mm, "end": v(91.36, 15.07) * mm});
            skLineSegment(sketch, "E38.15.9.2", {"start": v(86.73, 10.45) * mm, "end": v(86.73, 15.07) * mm});
            skLineSegment(sketch, "E38.15.9.3", {"start": v(91.36, 15.07) * mm, "end": v(86.73, 15.07) * mm});
            skLineSegment(sketch, "E38.15.10.0", {"start": v(91.36, 23.15) * mm, "end": v(86.73, 23.15) * mm});
            skLineSegment(sketch, "E38.15.10.1", {"start": v(91.36, 23.15) * mm, "end": v(91.36, 27.77) * mm});
            skLineSegment(sketch, "E38.15.10.2", {"start": v(86.73, 23.15) * mm, "end": v(86.73, 27.77) * mm});
            skLineSegment(sketch, "E38.15.10.3", {"start": v(91.36, 27.77) * mm, "end": v(86.73, 27.77) * mm});
            skLineSegment(sketch, "E38.15.11.0", {"start": v(91.36, 35.85) * mm, "end": v(86.73, 35.85) * mm});
            skLineSegment(sketch, "E38.15.11.1", {"start": v(91.36, 35.85) * mm, "end": v(91.36, 40.47) * mm});
            skLineSegment(sketch, "E38.15.11.2", {"start": v(86.73, 35.85) * mm, "end": v(86.73, 40.47) * mm});
            skLineSegment(sketch, "E38.15.11.3", {"start": v(91.36, 40.47) * mm, "end": v(86.73, 40.47) * mm});
            skLineSegment(sketch, "E38.15.12.0", {"start": v(91.36, 48.55) * mm, "end": v(86.73, 48.55) * mm});
            skLineSegment(sketch, "E38.15.12.1", {"start": v(91.36, 48.55) * mm, "end": v(91.36, 53.17) * mm});
            skLineSegment(sketch, "E38.15.12.2", {"start": v(86.73, 48.55) * mm, "end": v(86.73, 53.17) * mm});
            skLineSegment(sketch, "E38.15.12.3", {"start": v(91.36, 53.17) * mm, "end": v(86.73, 53.17) * mm});
            skLineSegment(sketch, "E38.15.13.0", {"start": v(91.36, 61.25) * mm, "end": v(86.73, 61.25) * mm});
            skLineSegment(sketch, "E38.15.13.1", {"start": v(91.36, 61.25) * mm, "end": v(91.36, 65.87) * mm});
            skLineSegment(sketch, "E38.15.13.2", {"start": v(86.73, 61.25) * mm, "end": v(86.73, 65.87) * mm});
            skLineSegment(sketch, "E38.15.13.3", {"start": v(91.36, 65.87) * mm, "end": v(86.73, 65.87) * mm});
            skLineSegment(sketch, "E38.15.14.0", {"start": v(91.36, 73.95) * mm, "end": v(86.73, 73.95) * mm});
            skLineSegment(sketch, "E38.15.14.1", {"start": v(91.36, 73.95) * mm, "end": v(91.36, 78.57) * mm});
            skLineSegment(sketch, "E38.15.14.2", {"start": v(86.73, 73.95) * mm, "end": v(86.73, 78.57) * mm});
            skLineSegment(sketch, "E38.15.14.3", {"start": v(91.36, 78.57) * mm, "end": v(86.73, 78.57) * mm});
            skLineSegment(sketch, "E38.15.15.0", {"start": v(91.36, 86.65) * mm, "end": v(86.73, 86.65) * mm});
            skLineSegment(sketch, "E38.15.15.1", {"start": v(91.36, 86.65) * mm, "end": v(91.36, 91.27) * mm});
            skLineSegment(sketch, "E38.15.15.2", {"start": v(86.73, 86.65) * mm, "end": v(86.73, 91.27) * mm});
            skLineSegment(sketch, "E38.15.15.3", {"start": v(91.36, 91.27) * mm, "end": v(86.73, 91.27) * mm});
            skLineSegment(sketch, "E38.15.16.0", {"start": v(91.36, 99.35) * mm, "end": v(86.73, 99.35) * mm});
            skLineSegment(sketch, "E38.15.16.1", {"start": v(91.36, 99.35) * mm, "end": v(91.36, 103.97) * mm});
            skLineSegment(sketch, "E38.15.16.2", {"start": v(86.73, 99.35) * mm, "end": v(86.73, 103.97) * mm});
            skLineSegment(sketch, "E38.15.16.3", {"start": v(91.36, 103.97) * mm, "end": v(86.73, 103.97) * mm});
            skLineSegment(sketch, "E38.16.0.0", {"start": v(104.06, -103.85) * mm, "end": v(99.43, -103.85) * mm});
            skLineSegment(sketch, "E38.16.0.1", {"start": v(104.06, -103.85) * mm, "end": v(104.06, -99.23) * mm});
            skLineSegment(sketch, "E38.16.0.2", {"start": v(99.43, -103.85) * mm, "end": v(99.43, -99.23) * mm});
            skLineSegment(sketch, "E38.16.0.3", {"start": v(104.06, -99.23) * mm, "end": v(99.43, -99.23) * mm});
            skLineSegment(sketch, "E38.16.1.0", {"start": v(104.06, -91.15) * mm, "end": v(99.43, -91.15) * mm});
            skLineSegment(sketch, "E38.16.1.1", {"start": v(104.06, -91.15) * mm, "end": v(104.06, -86.53) * mm});
            skLineSegment(sketch, "E38.16.1.2", {"start": v(99.43, -91.15) * mm, "end": v(99.43, -86.53) * mm});
            skLineSegment(sketch, "E38.16.1.3", {"start": v(104.06, -86.53) * mm, "end": v(99.43, -86.53) * mm});
            skLineSegment(sketch, "E38.16.2.0", {"start": v(104.06, -78.45) * mm, "end": v(99.43, -78.45) * mm});
            skLineSegment(sketch, "E38.16.2.1", {"start": v(104.06, -78.45) * mm, "end": v(104.06, -73.83) * mm});
            skLineSegment(sketch, "E38.16.2.2", {"start": v(99.43, -78.45) * mm, "end": v(99.43, -73.83) * mm});
            skLineSegment(sketch, "E38.16.2.3", {"start": v(104.06, -73.83) * mm, "end": v(99.43, -73.83) * mm});
            skLineSegment(sketch, "E38.16.3.0", {"start": v(104.06, -65.75) * mm, "end": v(99.43, -65.75) * mm});
            skLineSegment(sketch, "E38.16.3.1", {"start": v(104.06, -65.75) * mm, "end": v(104.06, -61.13) * mm});
            skLineSegment(sketch, "E38.16.3.2", {"start": v(99.43, -65.75) * mm, "end": v(99.43, -61.13) * mm});
            skLineSegment(sketch, "E38.16.3.3", {"start": v(104.06, -61.13) * mm, "end": v(99.43, -61.13) * mm});
            skLineSegment(sketch, "E38.16.4.0", {"start": v(104.06, -53.05) * mm, "end": v(99.43, -53.05) * mm});
            skLineSegment(sketch, "E38.16.4.1", {"start": v(104.06, -53.05) * mm, "end": v(104.06, -48.43) * mm});
            skLineSegment(sketch, "E38.16.4.2", {"start": v(99.43, -53.05) * mm, "end": v(99.43, -48.43) * mm});
            skLineSegment(sketch, "E38.16.4.3", {"start": v(104.06, -48.43) * mm, "end": v(99.43, -48.43) * mm});
            skLineSegment(sketch, "E38.16.5.0", {"start": v(104.06, -40.35) * mm, "end": v(99.43, -40.35) * mm});
            skLineSegment(sketch, "E38.16.5.1", {"start": v(104.06, -40.35) * mm, "end": v(104.06, -35.73) * mm});
            skLineSegment(sketch, "E38.16.5.2", {"start": v(99.43, -40.35) * mm, "end": v(99.43, -35.73) * mm});
            skLineSegment(sketch, "E38.16.5.3", {"start": v(104.06, -35.73) * mm, "end": v(99.43, -35.73) * mm});
            skLineSegment(sketch, "E38.16.6.0", {"start": v(104.06, -27.65) * mm, "end": v(99.43, -27.65) * mm});
            skLineSegment(sketch, "E38.16.6.1", {"start": v(104.06, -27.65) * mm, "end": v(104.06, -23.03) * mm});
            skLineSegment(sketch, "E38.16.6.2", {"start": v(99.43, -27.65) * mm, "end": v(99.43, -23.03) * mm});
            skLineSegment(sketch, "E38.16.6.3", {"start": v(104.06, -23.03) * mm, "end": v(99.43, -23.03) * mm});
            skLineSegment(sketch, "E38.16.7.0", {"start": v(104.06, -14.95) * mm, "end": v(99.43, -14.95) * mm});
            skLineSegment(sketch, "E38.16.7.1", {"start": v(104.06, -14.95) * mm, "end": v(104.06, -10.33) * mm});
            skLineSegment(sketch, "E38.16.7.2", {"start": v(99.43, -14.95) * mm, "end": v(99.43, -10.33) * mm});
            skLineSegment(sketch, "E38.16.7.3", {"start": v(104.06, -10.33) * mm, "end": v(99.43, -10.33) * mm});
            skLineSegment(sketch, "E38.16.8.0", {"start": v(104.06, -2.25) * mm, "end": v(99.43, -2.25) * mm});
            skLineSegment(sketch, "E38.16.8.1", {"start": v(104.06, -2.25) * mm, "end": v(104.06, 2.37) * mm});
            skLineSegment(sketch, "E38.16.8.2", {"start": v(99.43, -2.25) * mm, "end": v(99.43, 2.37) * mm});
            skLineSegment(sketch, "E38.16.8.3", {"start": v(104.06, 2.37) * mm, "end": v(99.43, 2.37) * mm});
            skLineSegment(sketch, "E38.16.9.0", {"start": v(104.06, 10.45) * mm, "end": v(99.43, 10.45) * mm});
            skLineSegment(sketch, "E38.16.9.1", {"start": v(104.06, 10.45) * mm, "end": v(104.06, 15.07) * mm});
            skLineSegment(sketch, "E38.16.9.2", {"start": v(99.43, 10.45) * mm, "end": v(99.43, 15.07) * mm});
            skLineSegment(sketch, "E38.16.9.3", {"start": v(104.06, 15.07) * mm, "end": v(99.43, 15.07) * mm});
            skLineSegment(sketch, "E38.16.10.0", {"start": v(104.06, 23.15) * mm, "end": v(99.43, 23.15) * mm});
            skLineSegment(sketch, "E38.16.10.1", {"start": v(104.06, 23.15) * mm, "end": v(104.06, 27.77) * mm});
            skLineSegment(sketch, "E38.16.10.2", {"start": v(99.43, 23.15) * mm, "end": v(99.43, 27.77) * mm});
            skLineSegment(sketch, "E38.16.10.3", {"start": v(104.06, 27.77) * mm, "end": v(99.43, 27.77) * mm});
            skLineSegment(sketch, "E38.16.11.0", {"start": v(104.06, 35.85) * mm, "end": v(99.43, 35.85) * mm});
            skLineSegment(sketch, "E38.16.11.1", {"start": v(104.06, 35.85) * mm, "end": v(104.06, 40.47) * mm});
            skLineSegment(sketch, "E38.16.11.2", {"start": v(99.43, 35.85) * mm, "end": v(99.43, 40.47) * mm});
            skLineSegment(sketch, "E38.16.11.3", {"start": v(104.06, 40.47) * mm, "end": v(99.43, 40.47) * mm});
            skLineSegment(sketch, "E38.16.12.0", {"start": v(104.06, 48.55) * mm, "end": v(99.43, 48.55) * mm});
            skLineSegment(sketch, "E38.16.12.1", {"start": v(104.06, 48.55) * mm, "end": v(104.06, 53.17) * mm});
            skLineSegment(sketch, "E38.16.12.2", {"start": v(99.43, 48.55) * mm, "end": v(99.43, 53.17) * mm});
            skLineSegment(sketch, "E38.16.12.3", {"start": v(104.06, 53.17) * mm, "end": v(99.43, 53.17) * mm});
            skLineSegment(sketch, "E38.16.13.0", {"start": v(104.06, 61.25) * mm, "end": v(99.43, 61.25) * mm});
            skLineSegment(sketch, "E38.16.13.1", {"start": v(104.06, 61.25) * mm, "end": v(104.06, 65.87) * mm});
            skLineSegment(sketch, "E38.16.13.2", {"start": v(99.43, 61.25) * mm, "end": v(99.43, 65.87) * mm});
            skLineSegment(sketch, "E38.16.13.3", {"start": v(104.06, 65.87) * mm, "end": v(99.43, 65.87) * mm});
            skLineSegment(sketch, "E38.16.14.0", {"start": v(104.06, 73.95) * mm, "end": v(99.43, 73.95) * mm});
            skLineSegment(sketch, "E38.16.14.1", {"start": v(104.06, 73.95) * mm, "end": v(104.06, 78.57) * mm});
            skLineSegment(sketch, "E38.16.14.2", {"start": v(99.43, 73.95) * mm, "end": v(99.43, 78.57) * mm});
            skLineSegment(sketch, "E38.16.14.3", {"start": v(104.06, 78.57) * mm, "end": v(99.43, 78.57) * mm});
            skLineSegment(sketch, "E38.16.15.0", {"start": v(104.06, 86.65) * mm, "end": v(99.43, 86.65) * mm});
            skLineSegment(sketch, "E38.16.15.1", {"start": v(104.06, 86.65) * mm, "end": v(104.06, 91.27) * mm});
            skLineSegment(sketch, "E38.16.15.2", {"start": v(99.43, 86.65) * mm, "end": v(99.43, 91.27) * mm});
            skLineSegment(sketch, "E38.16.15.3", {"start": v(104.06, 91.27) * mm, "end": v(99.43, 91.27) * mm});
            skLineSegment(sketch, "E38.16.16.0", {"start": v(104.06, 99.35) * mm, "end": v(99.43, 99.35) * mm});
            skLineSegment(sketch, "E38.16.16.1", {"start": v(104.06, 99.35) * mm, "end": v(104.06, 103.97) * mm});
            skLineSegment(sketch, "E38.16.16.2", {"start": v(99.43, 99.35) * mm, "end": v(99.43, 103.97) * mm});
            skLineSegment(sketch, "E38.16.16.3", {"start": v(104.06, 103.97) * mm, "end": v(99.43, 103.97) * mm});
            skLineSegment(sketch, "E38.direction1", {"start": v(-103.77, -103.85) * mm, "end": v(-91.07, -103.85) * mm, "construction": true});
            skLineSegment(sketch, "E38.direction2", {"start": v(-103.77, -103.85) * mm, "end": v(-103.77, -91.15) * mm, "construction": true});
            skSolve(sketch);
        }
        {
            var Q0;
            Q0=makeQuery(id+"F0.imprint","IMPRINT",FACE,{"disambiguationData":[TD([[makeQuery(id+"F0.imprint","IMPRINT",EDGE,{"derivedFrom":sQuery(id+"F0.wireOp",EDGE,"E0.top")}),-1.0]])]});
            extrude(context, id + "F1", {"entities" : qUnion([Q0]), "depth" : 3.17 * mm});
        }
    });
